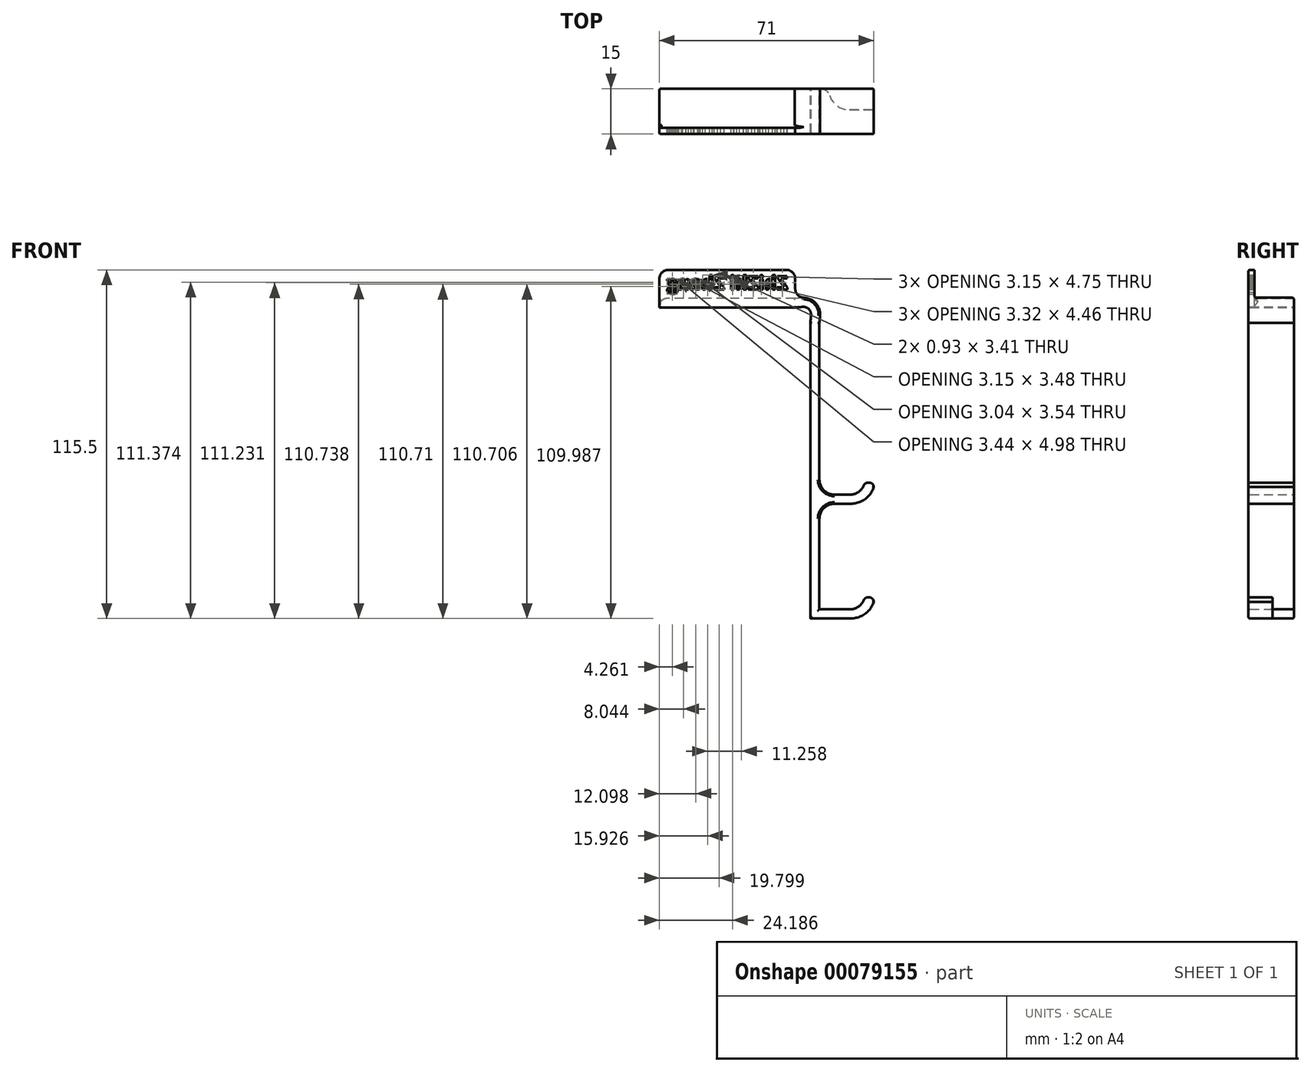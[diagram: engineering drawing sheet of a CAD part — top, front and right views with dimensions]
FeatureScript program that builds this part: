
annotation { "Feature Type Name" : "Feature", "Feature Type Description" : "" }
export const myFeature = defineFeature(function(context is Context, id is Id, definition is map)
    precondition{}
    {
        {
            var Q0;
            Q0=qCreatedBy(makeId("Front.planeOp"),FACE);
            var sketch = newSketch(context, id + "F0", { "sketchPlane" : qUnion([Q0])});
            skLineSegment(sketch, "E0.top", {"start": v(3, 3) * mm, "end": v(18, 3) * mm});
            skLineSegment(sketch, "E1.top", {"start": v(21, 7) * mm, "end": v(18, 7) * mm});
            skLineSegment(sketch, "E1.right", {"start": v(18, 3) * mm, "end": v(18, 7) * mm});
            skLineSegment(sketch, "E2", {"start": v(21, 7) * mm, "end": v(21, 0) * mm});
            skLineSegment(sketch, "E3", {"start": v(21, 0) * mm, "end": v(3, 0) * mm});
            skLineSegment(sketch, "E4.top", {"start": v(-5, 65) * mm, "end": v(-50, 65) * mm});
            skLineSegment(sketch, "E4.right", {"start": v(-50, 68) * mm, "end": v(-50, 65) * mm});
            skLineSegment(sketch, "E5", {"start": v(0, 65) * mm, "end": v(5.72, 70.72) * mm, "construction": true});
            skLineSegment(sketch, "E6", {"start": v(-5, 65) * mm, "end": v(0.5, 65.5) * mm});
            skLineSegment(sketch, "E7.MirrorCS", {"start": v(0, 60) * mm, "end": v(0.5, 65.5) * mm});
            skLineSegment(sketch, "E8", {"start": v(-5.14, 68) * mm, "end": v(3.81, 68.81) * mm});
            skLineSegment(sketch, "E9.MirrorCS", {"start": v(3, 59.86) * mm, "end": v(3.81, 68.81) * mm});
            skLineSegment(sketch, "E10", {"start": v(3, 3) * mm, "end": v(3, 59.86) * mm});
            skLineSegment(sketch, "E11.top", {"start": v(3, -35) * mm, "end": v(18, -35) * mm});
            skLineSegment(sketch, "E12.top", {"start": v(21, -31) * mm, "end": v(18, -31) * mm});
            skLineSegment(sketch, "E12.right", {"start": v(18, -35) * mm, "end": v(18, -31) * mm});
            skLineSegment(sketch, "E13", {"start": v(21, -31) * mm, "end": v(21, -38) * mm});
            skLineSegment(sketch, "E14", {"start": v(21, -38) * mm, "end": v(0, -38) * mm});
            skLineSegment(sketch, "E15", {"start": v(3, -35) * mm, "end": v(3, 0) * mm});
            skLineSegment(sketch, "E16", {"start": v(0, 60) * mm, "end": v(0, -38) * mm});
            skLineSegment(sketch, "E17", {"start": v(-5.14, 68) * mm, "end": v(-50, 68) * mm});
            skSolve(sketch);
        }
        {
            var Q0;
            Q0=qSketchRegion(id+"F0",true);
            extrude(context, id + "F1", {"entities" : qUnion([Q0]), "depth" : 15 * mm});
        }
        {
            var Q0;
            Q0=makeQuery(id+"F1.opExtrude","SWEPT_FACE",FACE,{"disambiguationData":[OSD([sQuery(id+"F0.wireOp",EDGE,"E11.top")])]});
            var sketch = newSketch(context, id + "F2", { "sketchPlane" : qUnion([Q0])});
            skLineSegment(sketch, "E18.0", {"start": v(21, -7) * mm, "end": v(21, 0) * mm});
            skLineSegment(sketch, "E19.bottom", {"start": v(6, 0) * mm, "end": v(21, 0) * mm});
            skLineSegment(sketch, "E19.top", {"start": v(6, -7) * mm, "end": v(21, -7) * mm});
            skLineSegment(sketch, "E19.left", {"start": v(6, 0) * mm, "end": v(6, -7) * mm});
            skLineSegment(sketch, "E19.right", {"start": v(21, 0) * mm, "end": v(21, -7) * mm});
            skPoint(sketch, "E20.orphan", {"position": v(21, -15) * mm});
            skSolve(sketch);
        }
        {
            var Q0;
            Q0 = qSketchRegion(id + "F2", true);
            extrude(context, id + "F3", {"entities" : qUnion([Q0]), "operationType" : NewBodyOperationType.REMOVE, "depth" : 25 * mm, "symmetric" : true});
        }
        {
            var Q0;
            Q0=makeQuery(id+"F1.opExtrude","SWEPT_EDGE",EDGE,{"disambiguationData":[OSD([sQuery(id+"F0.wireOp",EDGE,"VHxd6Wk6-jh9T-hKwV-plOy-LZrEurf6lyAQ.right"),sQuery(id+"F0.wireOp",EDGE,"E0.top")])]});
            var Q1;
            Q1=makeQuery(id+"F1.opExtrude","SWEPT_EDGE",EDGE,{"disambiguationData":[OSD([sQuery(id+"F0.wireOp",EDGE,"E0.top"),sQuery(id+"F0.wireOp",EDGE,"E1.right")])]});
            var Q2;
            Q2=makeQuery(id+"F1.opExtrude","SWEPT_EDGE",EDGE,{"disambiguationData":[OSD([sQuery(id+"F0.wireOp",EDGE,"E3"),sQuery(id+"F0.wireOp",EDGE,"E15")])]});
            var Q3;
            Q3=makeQuery(id+"F1.opExtrude","SWEPT_EDGE",EDGE,{"disambiguationData":[OSD([sQuery(id+"F0.wireOp",EDGE,"E11.top"),sQuery(id+"F0.wireOp",EDGE,"E12.right")])]});
            fillet(context, id + "F4", {"entities" : qUnion([Q0, Q1, Q2, Q3]), "radius" : 5 * mm, "tangentPropagation" : true, "allowEdgeOverflow" : false});
        }
        {
            var Q0;
            Q0=makeQuery(id+"F4.opFillet","BLEND_EDGE",EDGE,{"blendedFrom":[makeQuery(id+"F1.opExtrude","SWEPT_EDGE",EDGE,{"disambiguationData":[OSD([sQuery(id+"F0.wireOp",EDGE,"E0.top"),sQuery(id+"F0.wireOp",EDGE,"E1.right")])]}),makeQuery(id+"F1.opExtrude","SWEPT_FACE",FACE,{"disambiguationData":[OSD([sQuery(id+"F0.wireOp",EDGE,"E1.top")])]})],"blendedInto":[makeQuery(id+"F1.opExtrude","SWEPT_FACE",FACE,{"disambiguationData":[OSD([sQuery(id+"F0.wireOp",EDGE,"E1.top")])]})]});
            var Q1;
            Q1=makeQuery(id+"F1.opExtrude","SWEPT_EDGE",EDGE,{"disambiguationData":[OSD([sQuery(id+"F0.wireOp",EDGE,"E1.top"),sQuery(id+"F0.wireOp",EDGE,"E2")])]});
            var Q2;
            Q2=makeQuery(id+"F1.opExtrude","SWEPT_EDGE",EDGE,{"disambiguationData":[OSD([sQuery(id+"F0.wireOp",EDGE,"E12.top"),sQuery(id+"F0.wireOp",EDGE,"E13")])]});
            var Q3;
            Q3=makeQuery(id+"F4.opFillet","BLEND_EDGE",EDGE,{"blendedFrom":[makeQuery(id+"F1.opExtrude","SWEPT_EDGE",EDGE,{"disambiguationData":[OSD([sQuery(id+"F0.wireOp",EDGE,"E11.top"),sQuery(id+"F0.wireOp",EDGE,"E12.right")])]}),makeQuery(id+"F1.opExtrude","SWEPT_FACE",FACE,{"disambiguationData":[OSD([sQuery(id+"F0.wireOp",EDGE,"E12.top")])]})],"blendedInto":[makeQuery(id+"F1.opExtrude","SWEPT_FACE",FACE,{"disambiguationData":[OSD([sQuery(id+"F0.wireOp",EDGE,"E12.top")])]})]});
            fillet(context, id + "F5", {"entities" : qUnion([Q0, Q1, Q2, Q3]), "radius" : 1.5 * mm, "tangentPropagation" : true, "allowEdgeOverflow" : false});
        }
        {
            var Q0;
            Q0=makeQuery(id+"F1.opExtrude","SWEPT_EDGE",EDGE,{"disambiguationData":[OSD([sQuery(id+"F0.wireOp",EDGE,"E2"),sQuery(id+"F0.wireOp",EDGE,"E3")])]});
            var Q1;
            Q1=makeQuery(id+"F1.opExtrude","SWEPT_EDGE",EDGE,{"disambiguationData":[OSD([sQuery(id+"F0.wireOp",EDGE,"E13"),sQuery(id+"F0.wireOp",EDGE,"E14")])]});
            fillet(context, id + "F6", {"entities" : qUnion([Q0, Q1]), "radius" : 8 * mm, "tangentPropagation" : true, "allowEdgeOverflow" : false});
        }
        {
            var Q0;
            Q0=makeQuery(id+"F1.opExtrude","SWEPT_EDGE",EDGE,{"disambiguationData":[OSD([sQuery(id+"F0.wireOp",EDGE,"E6"),sQuery(id+"F0.wireOp",EDGE,"E7.MirrorCS")])]});
            fillet(context, id + "F7", {"entities" : qUnion([Q0]), "radius" : 2.5 * mm, "tangentPropagation" : true, "allowEdgeOverflow" : false});
        }
        {
            var Q0;
            Q0=makeQuery(id+"F1.opExtrude","SWEPT_EDGE",EDGE,{"disambiguationData":[OSD([sQuery(id+"F0.wireOp",EDGE,"E8"),sQuery(id+"F0.wireOp",EDGE,"E9.MirrorCS")])]});
            fillet(context, id + "F8", {"entities" : qUnion([Q0]), "radius" : 5.5 * mm, "tangentPropagation" : true, "allowEdgeOverflow" : false});
        }
        {
            var Q0;
            Q0=makeQuery(id+"F1.opExtrude","SWEPT_EDGE",EDGE,{"disambiguationData":[OSD([sQuery(id+"F0.wireOp",EDGE,"E4.right"),sQuery(id+"F0.wireOp",EDGE,"E17")])]});
            fillet(context, id + "F9", {"entities" : qUnion([Q0]), "radius" : 2.5 * mm, "tangentPropagation" : true, "allowEdgeOverflow" : false});
        }
        {
            var Q0;
            Q0=makeQuery(id+"FKw0b9sDwFtLhp3_1.boolean.opBoolean","COPY",EDGE,{"derivedFrom":makeQuery(id+"FKw0b9sDwFtLhp3_1.opExtrude","SWEPT_EDGE",EDGE,{"disambiguationData":[OSD([sQuery(id+"FaIadq1heUG16GC_1.wireOp",EDGE,"ajo2xejB-WB73-E7Yi-5oTq-upnxLA3L7wAk.top"),sQuery(id+"FaIadq1heUG16GC_1.wireOp",EDGE,"ajo2xejB-WB73-E7Yi-5oTq-upnxLA3L7wAk.left")])]})});
            var Q1;
            Q1=makeQuery(id+"F3.boolean.opBoolean","COPY",EDGE,{"derivedFrom":makeQuery(id+"F3.opExtrude","SWEPT_EDGE",EDGE,{"disambiguationData":[OSD([sQuery(id+"F2.wireOp",EDGE,"E19.top"),sQuery(id+"F2.wireOp",EDGE,"E19.left")])]})});
            fillet(context, id + "F10", {"entities" : qUnion([Q0, Q1]), "radius" : 7 * mm, "tangentPropagation" : true, "allowEdgeOverflow" : false});
        }
        {
            var Q0;
            Q0=makeQuery(id+"F1.opExtrude","CAP_FACE",FACE,{"disambiguationData":[OSD([sQuery(id+"F0.wireOp",EDGE,"E0.top"),sQuery(id+"F0.wireOp",EDGE,"E1.top"),sQuery(id+"F0.wireOp",EDGE,"E1.right"),sQuery(id+"F0.wireOp",EDGE,"E2"),sQuery(id+"F0.wireOp",EDGE,"E3"),sQuery(id+"F0.wireOp",EDGE,"E4.top"),sQuery(id+"F0.wireOp",EDGE,"E4.right"),sQuery(id+"F0.wireOp",EDGE,"E6"),sQuery(id+"F0.wireOp",EDGE,"E7.MirrorCS"),sQuery(id+"F0.wireOp",EDGE,"E8"),sQuery(id+"F0.wireOp",EDGE,"E9.MirrorCS"),sQuery(id+"F0.wireOp",EDGE,"E10"),sQuery(id+"F0.wireOp",EDGE,"E11.top"),sQuery(id+"F0.wireOp",EDGE,"E12.top"),sQuery(id+"F0.wireOp",EDGE,"E12.right"),sQuery(id+"F0.wireOp",EDGE,"E13"),sQuery(id+"F0.wireOp",EDGE,"E14"),sQuery(id+"F0.wireOp",EDGE,"E15"),sQuery(id+"F0.wireOp",EDGE,"E16"),sQuery(id+"F0.wireOp",EDGE,"E17")])],"isStart":false});
            var sketch = newSketch(context, id + "F11", { "sketchPlane" : qUnion([Q0])});
            skLineSegment(sketch, "E21.bottom", {"start": v(-5, 65.5) * mm, "end": v(-50, 65.5) * mm});
            skLineSegment(sketch, "E21.top", {"start": v(-5, 77.5) * mm, "end": v(-50, 77.5) * mm});
            skLineSegment(sketch, "E21.left", {"start": v(-50, 65.5) * mm, "end": v(-50, 77.5) * mm});
            skLineSegment(sketch, "E21.right", {"start": v(-5, 65.5) * mm, "end": v(-5, 77.5) * mm});
            skSolve(sketch);
        }
        {
            var Q0;
            Q0 = qSketchRegion(id + "F11", true);
            extrude(context, id + "F12", {"entities" : qUnion([Q0]), "operationType" : NewBodyOperationType.ADD, "oppositeDirection" : true, "depth" : 2 * mm});
        }
        {
            var Q0;
            Q0=makeQuery(id+"F12.opExtrude","SWEPT_EDGE",EDGE,{"disambiguationData":[OSD([sQuery(id+"F11.wireOp",EDGE,"E21.top"),sQuery(id+"F11.wireOp",EDGE,"E21.left")])]});
            var Q1;
            Q1=makeQuery(id+"F12.opExtrude","SWEPT_EDGE",EDGE,{"disambiguationData":[OSD([sQuery(id+"F11.wireOp",EDGE,"E21.top"),sQuery(id+"F11.wireOp",EDGE,"E21.right")])]});
            fillet(context, id + "F13", {"entities" : qUnion([Q0, Q1]), "radius" : 3 * mm, "tangentPropagation" : true, "allowEdgeOverflow" : false});
        }
        {
            var Q0;
            Q0=makeQuery(id+"F12.boolean.opBoolean","INTERSECT",EDGE,{"derivedFrom":[makeQuery(id+"F1.opExtrude","SWEPT_FACE",FACE,{"disambiguationData":[OSD([sQuery(id+"F0.wireOp",EDGE,"E17")])]}),makeQuery(id+"F12.opExtrude","CAP_FACE",FACE,{"disambiguationData":[OSD([sQuery(id+"F11.wireOp",EDGE,"E21.bottom"),sQuery(id+"F11.wireOp",EDGE,"E21.top"),sQuery(id+"F11.wireOp",EDGE,"E21.left"),sQuery(id+"F11.wireOp",EDGE,"E21.right")])],"isStart":false})]});
            var Q1;
            Q1=makeQuery(id+"F12.boolean.opBoolean","INTERSECT",EDGE,{"derivedFrom":[makeQuery(id+"F9.opFillet","BLEND_FACE",FACE,{"disambiguationData":[OSD([sQuery(id+"F0.wireOp",EDGE,"E4.right"),sQuery(id+"F0.wireOp",EDGE,"E17")])]}),makeQuery(id+"F12.opExtrude","CAP_FACE",FACE,{"disambiguationData":[OSD([sQuery(id+"F11.wireOp",EDGE,"E21.bottom"),sQuery(id+"F11.wireOp",EDGE,"E21.top"),sQuery(id+"F11.wireOp",EDGE,"E21.left"),sQuery(id+"F11.wireOp",EDGE,"E21.right")])],"isStart":false})]});
            fillet(context, id + "F14", {"entities" : qUnion([Q0, Q1]), "radius" : 1 * mm, "tangentPropagation" : true, "allowEdgeOverflow" : false});
        }
        {
            var Q0;
            Q0=makeQuery(id+"F12.boolean.opBoolean","INTERSECT",EDGE,{"derivedFrom":[makeQuery(id+"F1.opExtrude","SWEPT_FACE",FACE,{"disambiguationData":[OSD([sQuery(id+"F0.wireOp",EDGE,"E8")])]}),makeQuery(id+"F12.opExtrude","SWEPT_FACE",FACE,{"disambiguationData":[OSD([sQuery(id+"F11.wireOp",EDGE,"E21.right")])]})]});
            fillet(context, id + "F15", {"entities" : qUnion([Q0]), "radius" : 3 * mm, "tangentPropagation" : true, "allowEdgeOverflow" : false});
        }
        {
            var Q0;
            Q0=makeQuery(id+"F10.opFillet","BLEND_EDGE",EDGE,{"blendedFrom":[makeQuery(id+"FKw0b9sDwFtLhp3_1.boolean.opBoolean","COPY",EDGE,{"derivedFrom":makeQuery(id+"FKw0b9sDwFtLhp3_1.opExtrude","SWEPT_EDGE",EDGE,{"disambiguationData":[OSD([sQuery(id+"FaIadq1heUG16GC_1.wireOp",EDGE,"ajo2xejB-WB73-E7Yi-5oTq-upnxLA3L7wAk.top"),sQuery(id+"FaIadq1heUG16GC_1.wireOp",EDGE,"ajo2xejB-WB73-E7Yi-5oTq-upnxLA3L7wAk.left")])]})}),makeQuery(id+"F1.opExtrude","CAP_FACE",FACE,{"disambiguationData":[OSD([sQuery(id+"F0.wireOp",EDGE,"E0.top"),sQuery(id+"F0.wireOp",EDGE,"E1.top"),sQuery(id+"F0.wireOp",EDGE,"E1.right"),sQuery(id+"F0.wireOp",EDGE,"E2"),sQuery(id+"F0.wireOp",EDGE,"E3"),sQuery(id+"F0.wireOp",EDGE,"E4.top"),sQuery(id+"F0.wireOp",EDGE,"E4.right"),sQuery(id+"F0.wireOp",EDGE,"E6"),sQuery(id+"F0.wireOp",EDGE,"E7.MirrorCS"),sQuery(id+"F0.wireOp",EDGE,"E8"),sQuery(id+"F0.wireOp",EDGE,"E9.MirrorCS"),sQuery(id+"F0.wireOp",EDGE,"E10"),sQuery(id+"F0.wireOp",EDGE,"E11.top"),sQuery(id+"F0.wireOp",EDGE,"E12.top"),sQuery(id+"F0.wireOp",EDGE,"E12.right"),sQuery(id+"F0.wireOp",EDGE,"E13"),sQuery(id+"F0.wireOp",EDGE,"E14"),sQuery(id+"F0.wireOp",EDGE,"E15"),sQuery(id+"F0.wireOp",EDGE,"E16"),sQuery(id+"F0.wireOp",EDGE,"E17")])],"isStart":false})],"blendedInto":[makeQuery(id+"F1.opExtrude","CAP_FACE",FACE,{"disambiguationData":[OSD([sQuery(id+"F0.wireOp",EDGE,"E0.top"),sQuery(id+"F0.wireOp",EDGE,"E1.top"),sQuery(id+"F0.wireOp",EDGE,"E1.right"),sQuery(id+"F0.wireOp",EDGE,"E2"),sQuery(id+"F0.wireOp",EDGE,"E3"),sQuery(id+"F0.wireOp",EDGE,"E4.top"),sQuery(id+"F0.wireOp",EDGE,"E4.right"),sQuery(id+"F0.wireOp",EDGE,"E6"),sQuery(id+"F0.wireOp",EDGE,"E7.MirrorCS"),sQuery(id+"F0.wireOp",EDGE,"E8"),sQuery(id+"F0.wireOp",EDGE,"E9.MirrorCS"),sQuery(id+"F0.wireOp",EDGE,"E10"),sQuery(id+"F0.wireOp",EDGE,"E11.top"),sQuery(id+"F0.wireOp",EDGE,"E12.top"),sQuery(id+"F0.wireOp",EDGE,"E12.right"),sQuery(id+"F0.wireOp",EDGE,"E13"),sQuery(id+"F0.wireOp",EDGE,"E14"),sQuery(id+"F0.wireOp",EDGE,"E15"),sQuery(id+"F0.wireOp",EDGE,"E16"),sQuery(id+"F0.wireOp",EDGE,"E17")])],"isStart":false})]});
            var Q1;
            Q1=makeQuery(id+"F10.opFillet","BLEND_EDGE",EDGE,{"blendedFrom":[makeQuery(id+"F3.boolean.opBoolean","COPY",EDGE,{"derivedFrom":makeQuery(id+"F3.opExtrude","SWEPT_EDGE",EDGE,{"disambiguationData":[OSD([sQuery(id+"F2.wireOp",EDGE,"E19.top"),sQuery(id+"F2.wireOp",EDGE,"E19.left")])]})}),makeQuery(id+"F1.opExtrude","CAP_FACE",FACE,{"disambiguationData":[OSD([sQuery(id+"F0.wireOp",EDGE,"E0.top"),sQuery(id+"F0.wireOp",EDGE,"E1.top"),sQuery(id+"F0.wireOp",EDGE,"E1.right"),sQuery(id+"F0.wireOp",EDGE,"E2"),sQuery(id+"F0.wireOp",EDGE,"E3"),sQuery(id+"F0.wireOp",EDGE,"E4.top"),sQuery(id+"F0.wireOp",EDGE,"E4.right"),sQuery(id+"F0.wireOp",EDGE,"E6"),sQuery(id+"F0.wireOp",EDGE,"E7.MirrorCS"),sQuery(id+"F0.wireOp",EDGE,"E8"),sQuery(id+"F0.wireOp",EDGE,"E9.MirrorCS"),sQuery(id+"F0.wireOp",EDGE,"E10"),sQuery(id+"F0.wireOp",EDGE,"E11.top"),sQuery(id+"F0.wireOp",EDGE,"E12.top"),sQuery(id+"F0.wireOp",EDGE,"E12.right"),sQuery(id+"F0.wireOp",EDGE,"E13"),sQuery(id+"F0.wireOp",EDGE,"E14"),sQuery(id+"F0.wireOp",EDGE,"E15"),sQuery(id+"F0.wireOp",EDGE,"E16"),sQuery(id+"F0.wireOp",EDGE,"E17")])],"isStart":true})],"blendedInto":[makeQuery(id+"F1.opExtrude","CAP_FACE",FACE,{"disambiguationData":[OSD([sQuery(id+"F0.wireOp",EDGE,"E0.top"),sQuery(id+"F0.wireOp",EDGE,"E1.top"),sQuery(id+"F0.wireOp",EDGE,"E1.right"),sQuery(id+"F0.wireOp",EDGE,"E2"),sQuery(id+"F0.wireOp",EDGE,"E3"),sQuery(id+"F0.wireOp",EDGE,"E4.top"),sQuery(id+"F0.wireOp",EDGE,"E4.right"),sQuery(id+"F0.wireOp",EDGE,"E6"),sQuery(id+"F0.wireOp",EDGE,"E7.MirrorCS"),sQuery(id+"F0.wireOp",EDGE,"E8"),sQuery(id+"F0.wireOp",EDGE,"E9.MirrorCS"),sQuery(id+"F0.wireOp",EDGE,"E10"),sQuery(id+"F0.wireOp",EDGE,"E11.top"),sQuery(id+"F0.wireOp",EDGE,"E12.top"),sQuery(id+"F0.wireOp",EDGE,"E12.right"),sQuery(id+"F0.wireOp",EDGE,"E13"),sQuery(id+"F0.wireOp",EDGE,"E14"),sQuery(id+"F0.wireOp",EDGE,"E15"),sQuery(id+"F0.wireOp",EDGE,"E16"),sQuery(id+"F0.wireOp",EDGE,"E17")])],"isStart":true})]});
            fillet(context, id + "F16", {"entities" : qUnion([Q0, Q1]), "radius" : 3 * mm, "tangentPropagation" : true, "allowEdgeOverflow" : false});
        }
        {
            var Q0;
            Q0=makeQuery(id+"F12.opExtrude","CAP_FACE",FACE,{"disambiguationData":[OSD([sQuery(id+"F11.wireOp",EDGE,"E21.bottom"),sQuery(id+"F11.wireOp",EDGE,"E21.top"),sQuery(id+"F11.wireOp",EDGE,"E21.left"),sQuery(id+"F11.wireOp",EDGE,"E21.right")])],"isStart":false});
            var sketch = newSketch(context, id + "F17", { "sketchPlane" : qUnion([Q0])});
            skText(sketch, "E22", { "text": "ZhiZhi Zhang", "fontName": "OpenSans-Bold.ttf"});
            const initialGuessF17  = {"E22": [0.0075, 0.071, 1, 0, 0.0045]};
            skSetInitialGuess(sketch, initialGuessF17);
            skSolve(sketch);
        }
        {
            var Q0;
            Q0 = qSketchRegion(id + "F17", true);
            extrude(context, id + "F18", {"entities" : qUnion([Q0]), "operationType" : NewBodyOperationType.REMOVE, "endBound" : BoundingType.UP_TO_NEXT, "oppositeDirection" : true, "depth" : 25 * mm});
        }
        {
            var Q0;
            Q0=makeQuery(id+"F1.opExtrude","CAP_EDGE",EDGE,{"disambiguationData":[OSD([sQuery(id+"F0.wireOp",EDGE,"E10")])],"isStart":true});
            var Q1;
            {var subQ0=sQuery(id+"F0.wireOp",EDGE,"E10");var subQ1=sQuery(id+"F0.wireOp",EDGE,"E0.top");Q1=makeQuery(id+"F4.opFillet","BLEND_EDGE",EDGE,{"blendedFrom":[makeQuery(id+"F1.opExtrude","SWEPT_EDGE",EDGE,{"disambiguationData":[OSD([subQ1,subQ0])]}),makeQuery(id+"F1.opExtrude","CAP_FACE",FACE,{"disambiguationData":[OSD([subQ1,sQuery(id+"F0.wireOp",EDGE,"E1.top"),sQuery(id+"F0.wireOp",EDGE,"E1.right"),sQuery(id+"F0.wireOp",EDGE,"E2"),sQuery(id+"F0.wireOp",EDGE,"E3"),sQuery(id+"F0.wireOp",EDGE,"E4.top"),sQuery(id+"F0.wireOp",EDGE,"E4.right"),sQuery(id+"F0.wireOp",EDGE,"E6"),sQuery(id+"F0.wireOp",EDGE,"E7.MirrorCS"),sQuery(id+"F0.wireOp",EDGE,"E8"),sQuery(id+"F0.wireOp",EDGE,"E9.MirrorCS"),subQ0,sQuery(id+"F0.wireOp",EDGE,"E11.top"),sQuery(id+"F0.wireOp",EDGE,"E12.top"),sQuery(id+"F0.wireOp",EDGE,"E12.right"),sQuery(id+"F0.wireOp",EDGE,"E13"),sQuery(id+"F0.wireOp",EDGE,"E14"),sQuery(id+"F0.wireOp",EDGE,"E15"),sQuery(id+"F0.wireOp",EDGE,"E16"),sQuery(id+"F0.wireOp",EDGE,"E17")])],"isStart":true})],"blendedInto":[makeQuery(id+"F1.opExtrude","CAP_FACE",FACE,{"disambiguationData":[OSD([subQ1,sQuery(id+"F0.wireOp",EDGE,"E1.top"),sQuery(id+"F0.wireOp",EDGE,"E1.right"),sQuery(id+"F0.wireOp",EDGE,"E2"),sQuery(id+"F0.wireOp",EDGE,"E3"),sQuery(id+"F0.wireOp",EDGE,"E4.top"),sQuery(id+"F0.wireOp",EDGE,"E4.right"),sQuery(id+"F0.wireOp",EDGE,"E6"),sQuery(id+"F0.wireOp",EDGE,"E7.MirrorCS"),sQuery(id+"F0.wireOp",EDGE,"E8"),sQuery(id+"F0.wireOp",EDGE,"E9.MirrorCS"),subQ0,sQuery(id+"F0.wireOp",EDGE,"E11.top"),sQuery(id+"F0.wireOp",EDGE,"E12.top"),sQuery(id+"F0.wireOp",EDGE,"E12.right"),sQuery(id+"F0.wireOp",EDGE,"E13"),sQuery(id+"F0.wireOp",EDGE,"E14"),sQuery(id+"F0.wireOp",EDGE,"E15"),sQuery(id+"F0.wireOp",EDGE,"E16"),sQuery(id+"F0.wireOp",EDGE,"E17")])],"isStart":true})]});}
            var Q2;
            Q2=makeQuery(id+"F1.opExtrude","CAP_EDGE",EDGE,{"disambiguationData":[OSD([sQuery(id+"F0.wireOp",EDGE,"E9.MirrorCS")])],"isStart":true});
            var Q3;
            {var subQ0=sQuery(id+"F0.wireOp",EDGE,"E9.MirrorCS");var subQ1=sQuery(id+"F0.wireOp",EDGE,"E8");Q3=makeQuery(id+"F8.opFillet","BLEND_EDGE",EDGE,{"blendedFrom":[makeQuery(id+"F1.opExtrude","SWEPT_EDGE",EDGE,{"disambiguationData":[OSD([subQ1,subQ0])]}),makeQuery(id+"F1.opExtrude","CAP_FACE",FACE,{"disambiguationData":[OSD([sQuery(id+"F0.wireOp",EDGE,"E0.top"),sQuery(id+"F0.wireOp",EDGE,"E1.top"),sQuery(id+"F0.wireOp",EDGE,"E1.right"),sQuery(id+"F0.wireOp",EDGE,"E2"),sQuery(id+"F0.wireOp",EDGE,"E3"),sQuery(id+"F0.wireOp",EDGE,"E4.top"),sQuery(id+"F0.wireOp",EDGE,"E4.right"),sQuery(id+"F0.wireOp",EDGE,"E6"),sQuery(id+"F0.wireOp",EDGE,"E7.MirrorCS"),subQ1,subQ0,sQuery(id+"F0.wireOp",EDGE,"E10"),sQuery(id+"F0.wireOp",EDGE,"E11.top"),sQuery(id+"F0.wireOp",EDGE,"E12.top"),sQuery(id+"F0.wireOp",EDGE,"E12.right"),sQuery(id+"F0.wireOp",EDGE,"E13"),sQuery(id+"F0.wireOp",EDGE,"E14"),sQuery(id+"F0.wireOp",EDGE,"E15"),sQuery(id+"F0.wireOp",EDGE,"E16"),sQuery(id+"F0.wireOp",EDGE,"E17")])],"isStart":true})],"blendedInto":[makeQuery(id+"F1.opExtrude","CAP_FACE",FACE,{"disambiguationData":[OSD([sQuery(id+"F0.wireOp",EDGE,"E0.top"),sQuery(id+"F0.wireOp",EDGE,"E1.top"),sQuery(id+"F0.wireOp",EDGE,"E1.right"),sQuery(id+"F0.wireOp",EDGE,"E2"),sQuery(id+"F0.wireOp",EDGE,"E3"),sQuery(id+"F0.wireOp",EDGE,"E4.top"),sQuery(id+"F0.wireOp",EDGE,"E4.right"),sQuery(id+"F0.wireOp",EDGE,"E6"),sQuery(id+"F0.wireOp",EDGE,"E7.MirrorCS"),subQ1,subQ0,sQuery(id+"F0.wireOp",EDGE,"E10"),sQuery(id+"F0.wireOp",EDGE,"E11.top"),sQuery(id+"F0.wireOp",EDGE,"E12.top"),sQuery(id+"F0.wireOp",EDGE,"E12.right"),sQuery(id+"F0.wireOp",EDGE,"E13"),sQuery(id+"F0.wireOp",EDGE,"E14"),sQuery(id+"F0.wireOp",EDGE,"E15"),sQuery(id+"F0.wireOp",EDGE,"E16"),sQuery(id+"F0.wireOp",EDGE,"E17")])],"isStart":true})]});}
            var Q4;
            Q4=makeQuery(id+"F1.opExtrude","CAP_EDGE",EDGE,{"disambiguationData":[OSD([sQuery(id+"F0.wireOp",EDGE,"E8")])],"isStart":true});
            var Q5;
            Q5=makeQuery(id+"F1.opExtrude","CAP_EDGE",EDGE,{"disambiguationData":[OSD([sQuery(id+"F0.wireOp",EDGE,"E17")])],"isStart":true});
            var Q6;
            {var subQ0=sQuery(id+"F0.wireOp",EDGE,"E17");var subQ1=sQuery(id+"F0.wireOp",EDGE,"E4.right");Q6=makeQuery(id+"F9.opFillet","BLEND_EDGE",EDGE,{"blendedFrom":[makeQuery(id+"F1.opExtrude","SWEPT_EDGE",EDGE,{"disambiguationData":[OSD([subQ1,subQ0])]}),makeQuery(id+"F1.opExtrude","CAP_FACE",FACE,{"disambiguationData":[OSD([sQuery(id+"F0.wireOp",EDGE,"E0.top"),sQuery(id+"F0.wireOp",EDGE,"E1.top"),sQuery(id+"F0.wireOp",EDGE,"E1.right"),sQuery(id+"F0.wireOp",EDGE,"E2"),sQuery(id+"F0.wireOp",EDGE,"E3"),sQuery(id+"F0.wireOp",EDGE,"E4.top"),subQ1,sQuery(id+"F0.wireOp",EDGE,"E6"),sQuery(id+"F0.wireOp",EDGE,"E7.MirrorCS"),sQuery(id+"F0.wireOp",EDGE,"E8"),sQuery(id+"F0.wireOp",EDGE,"E9.MirrorCS"),sQuery(id+"F0.wireOp",EDGE,"E10"),sQuery(id+"F0.wireOp",EDGE,"E11.top"),sQuery(id+"F0.wireOp",EDGE,"E12.top"),sQuery(id+"F0.wireOp",EDGE,"E12.right"),sQuery(id+"F0.wireOp",EDGE,"E13"),sQuery(id+"F0.wireOp",EDGE,"E14"),sQuery(id+"F0.wireOp",EDGE,"E15"),sQuery(id+"F0.wireOp",EDGE,"E16"),subQ0])],"isStart":true})],"blendedInto":[makeQuery(id+"F1.opExtrude","CAP_FACE",FACE,{"disambiguationData":[OSD([sQuery(id+"F0.wireOp",EDGE,"E0.top"),sQuery(id+"F0.wireOp",EDGE,"E1.top"),sQuery(id+"F0.wireOp",EDGE,"E1.right"),sQuery(id+"F0.wireOp",EDGE,"E2"),sQuery(id+"F0.wireOp",EDGE,"E3"),sQuery(id+"F0.wireOp",EDGE,"E4.top"),subQ1,sQuery(id+"F0.wireOp",EDGE,"E6"),sQuery(id+"F0.wireOp",EDGE,"E7.MirrorCS"),sQuery(id+"F0.wireOp",EDGE,"E8"),sQuery(id+"F0.wireOp",EDGE,"E9.MirrorCS"),sQuery(id+"F0.wireOp",EDGE,"E10"),sQuery(id+"F0.wireOp",EDGE,"E11.top"),sQuery(id+"F0.wireOp",EDGE,"E12.top"),sQuery(id+"F0.wireOp",EDGE,"E12.right"),sQuery(id+"F0.wireOp",EDGE,"E13"),sQuery(id+"F0.wireOp",EDGE,"E14"),sQuery(id+"F0.wireOp",EDGE,"E15"),sQuery(id+"F0.wireOp",EDGE,"E16"),subQ0])],"isStart":true})]});}
            var Q7;
            Q7=makeQuery(id+"F1.opExtrude","CAP_EDGE",EDGE,{"disambiguationData":[OSD([sQuery(id+"F0.wireOp",EDGE,"E4.top")])],"isStart":true});
            var Q8;
            Q8=makeQuery(id+"F1.opExtrude","CAP_EDGE",EDGE,{"disambiguationData":[OSD([sQuery(id+"F0.wireOp",EDGE,"E4.right")])],"isStart":true});
            var Q9;
            Q9=makeQuery(id+"F1.opExtrude","CAP_EDGE",EDGE,{"disambiguationData":[OSD([sQuery(id+"F0.wireOp",EDGE,"E6")])],"isStart":true});
            var Q10;
            {var subQ0=sQuery(id+"F0.wireOp",EDGE,"E7.MirrorCS");var subQ1=sQuery(id+"F0.wireOp",EDGE,"E6");Q10=makeQuery(id+"F7.opFillet","BLEND_EDGE",EDGE,{"blendedFrom":[makeQuery(id+"F1.opExtrude","SWEPT_EDGE",EDGE,{"disambiguationData":[OSD([subQ1,subQ0])]}),makeQuery(id+"F1.opExtrude","CAP_FACE",FACE,{"disambiguationData":[OSD([sQuery(id+"F0.wireOp",EDGE,"E0.top"),sQuery(id+"F0.wireOp",EDGE,"E1.top"),sQuery(id+"F0.wireOp",EDGE,"E1.right"),sQuery(id+"F0.wireOp",EDGE,"E2"),sQuery(id+"F0.wireOp",EDGE,"E3"),sQuery(id+"F0.wireOp",EDGE,"E4.top"),sQuery(id+"F0.wireOp",EDGE,"E4.right"),subQ1,subQ0,sQuery(id+"F0.wireOp",EDGE,"E8"),sQuery(id+"F0.wireOp",EDGE,"E9.MirrorCS"),sQuery(id+"F0.wireOp",EDGE,"E10"),sQuery(id+"F0.wireOp",EDGE,"E11.top"),sQuery(id+"F0.wireOp",EDGE,"E12.top"),sQuery(id+"F0.wireOp",EDGE,"E12.right"),sQuery(id+"F0.wireOp",EDGE,"E13"),sQuery(id+"F0.wireOp",EDGE,"E14"),sQuery(id+"F0.wireOp",EDGE,"E15"),sQuery(id+"F0.wireOp",EDGE,"E16"),sQuery(id+"F0.wireOp",EDGE,"E17")])],"isStart":true})],"blendedInto":[makeQuery(id+"F1.opExtrude","CAP_FACE",FACE,{"disambiguationData":[OSD([sQuery(id+"F0.wireOp",EDGE,"E0.top"),sQuery(id+"F0.wireOp",EDGE,"E1.top"),sQuery(id+"F0.wireOp",EDGE,"E1.right"),sQuery(id+"F0.wireOp",EDGE,"E2"),sQuery(id+"F0.wireOp",EDGE,"E3"),sQuery(id+"F0.wireOp",EDGE,"E4.top"),sQuery(id+"F0.wireOp",EDGE,"E4.right"),subQ1,subQ0,sQuery(id+"F0.wireOp",EDGE,"E8"),sQuery(id+"F0.wireOp",EDGE,"E9.MirrorCS"),sQuery(id+"F0.wireOp",EDGE,"E10"),sQuery(id+"F0.wireOp",EDGE,"E11.top"),sQuery(id+"F0.wireOp",EDGE,"E12.top"),sQuery(id+"F0.wireOp",EDGE,"E12.right"),sQuery(id+"F0.wireOp",EDGE,"E13"),sQuery(id+"F0.wireOp",EDGE,"E14"),sQuery(id+"F0.wireOp",EDGE,"E15"),sQuery(id+"F0.wireOp",EDGE,"E16"),sQuery(id+"F0.wireOp",EDGE,"E17")])],"isStart":true})]});}
            var Q11;
            Q11=makeQuery(id+"F1.opExtrude","CAP_EDGE",EDGE,{"disambiguationData":[OSD([sQuery(id+"F0.wireOp",EDGE,"E7.MirrorCS")])],"isStart":true});
            var Q12;
            Q12=makeQuery(id+"F1.opExtrude","CAP_EDGE",EDGE,{"disambiguationData":[OSD([sQuery(id+"F0.wireOp",EDGE,"E16")])],"isStart":true});
            var Q13;
            Q13=makeQuery(id+"F1.opExtrude","CAP_EDGE",EDGE,{"disambiguationData":[OSD([sQuery(id+"F0.wireOp",EDGE,"E14")])],"isStart":true});
            var Q14;
            {var subQ0=sQuery(id+"F0.wireOp",EDGE,"E14");Q14=makeQuery(id+"F16.opFillet","BLEND_EDGE",EDGE,{"blendedFrom":[makeQuery(id+"F10.opFillet","BLEND_EDGE",EDGE,{"blendedFrom":[makeQuery(id+"F3.boolean.opBoolean","COPY",EDGE,{"derivedFrom":makeQuery(id+"F3.opExtrude","SWEPT_EDGE",EDGE,{"disambiguationData":[OSD([sQuery(id+"F2.wireOp",EDGE,"E19.top"),sQuery(id+"F2.wireOp",EDGE,"E19.left")])]})}),makeQuery(id+"F1.opExtrude","CAP_FACE",FACE,{"disambiguationData":[OSD([sQuery(id+"F0.wireOp",EDGE,"E0.top"),sQuery(id+"F0.wireOp",EDGE,"E1.top"),sQuery(id+"F0.wireOp",EDGE,"E1.right"),sQuery(id+"F0.wireOp",EDGE,"E2"),sQuery(id+"F0.wireOp",EDGE,"E3"),sQuery(id+"F0.wireOp",EDGE,"E4.top"),sQuery(id+"F0.wireOp",EDGE,"E4.right"),sQuery(id+"F0.wireOp",EDGE,"E6"),sQuery(id+"F0.wireOp",EDGE,"E7.MirrorCS"),sQuery(id+"F0.wireOp",EDGE,"E8"),sQuery(id+"F0.wireOp",EDGE,"E9.MirrorCS"),sQuery(id+"F0.wireOp",EDGE,"E10"),sQuery(id+"F0.wireOp",EDGE,"E11.top"),sQuery(id+"F0.wireOp",EDGE,"E12.top"),sQuery(id+"F0.wireOp",EDGE,"E12.right"),sQuery(id+"F0.wireOp",EDGE,"E13"),subQ0,sQuery(id+"F0.wireOp",EDGE,"E15"),sQuery(id+"F0.wireOp",EDGE,"E16"),sQuery(id+"F0.wireOp",EDGE,"E17")])],"isStart":true})],"blendedInto":[makeQuery(id+"F1.opExtrude","CAP_FACE",FACE,{"disambiguationData":[OSD([sQuery(id+"F0.wireOp",EDGE,"E0.top"),sQuery(id+"F0.wireOp",EDGE,"E1.top"),sQuery(id+"F0.wireOp",EDGE,"E1.right"),sQuery(id+"F0.wireOp",EDGE,"E2"),sQuery(id+"F0.wireOp",EDGE,"E3"),sQuery(id+"F0.wireOp",EDGE,"E4.top"),sQuery(id+"F0.wireOp",EDGE,"E4.right"),sQuery(id+"F0.wireOp",EDGE,"E6"),sQuery(id+"F0.wireOp",EDGE,"E7.MirrorCS"),sQuery(id+"F0.wireOp",EDGE,"E8"),sQuery(id+"F0.wireOp",EDGE,"E9.MirrorCS"),sQuery(id+"F0.wireOp",EDGE,"E10"),sQuery(id+"F0.wireOp",EDGE,"E11.top"),sQuery(id+"F0.wireOp",EDGE,"E12.top"),sQuery(id+"F0.wireOp",EDGE,"E12.right"),sQuery(id+"F0.wireOp",EDGE,"E13"),subQ0,sQuery(id+"F0.wireOp",EDGE,"E15"),sQuery(id+"F0.wireOp",EDGE,"E16"),sQuery(id+"F0.wireOp",EDGE,"E17")])],"isStart":true})]}),makeQuery(id+"F1.opExtrude","SWEPT_FACE",FACE,{"disambiguationData":[OSD([subQ0])]})],"blendedInto":[makeQuery(id+"F1.opExtrude","SWEPT_FACE",FACE,{"disambiguationData":[OSD([subQ0])]})]});}
            var Q15;
            Q15=makeQuery(id+"F10.opFillet","BLEND_EDGE",EDGE,{"blendedFrom":[makeQuery(id+"F3.boolean.opBoolean","COPY",EDGE,{"derivedFrom":makeQuery(id+"F3.opExtrude","SWEPT_EDGE",EDGE,{"disambiguationData":[OSD([sQuery(id+"F2.wireOp",EDGE,"E19.top"),sQuery(id+"F2.wireOp",EDGE,"E19.left")])]})}),makeQuery(id+"F1.opExtrude","SWEPT_FACE",FACE,{"disambiguationData":[OSD([sQuery(id+"F0.wireOp",EDGE,"E14")])]})],"blendedInto":[makeQuery(id+"F1.opExtrude","SWEPT_FACE",FACE,{"disambiguationData":[OSD([sQuery(id+"F0.wireOp",EDGE,"E14")])]})]});
            var Q16;
            Q16=makeQuery(id+"F6.opFillet","BLEND_EDGE",EDGE,{"blendedFrom":[makeQuery(id+"F1.opExtrude","SWEPT_EDGE",EDGE,{"disambiguationData":[OSD([sQuery(id+"F0.wireOp",EDGE,"E13"),sQuery(id+"F0.wireOp",EDGE,"E14")])]}),makeQuery(id+"F3.boolean.opBoolean","COPY",FACE,{"derivedFrom":makeQuery(id+"F3.opExtrude","SWEPT_FACE",FACE,{"disambiguationData":[OSD([sQuery(id+"F2.wireOp",EDGE,"E19.top")])]})})],"blendedInto":[makeQuery(id+"F3.boolean.opBoolean","COPY",FACE,{"derivedFrom":makeQuery(id+"F3.opExtrude","SWEPT_FACE",FACE,{"disambiguationData":[OSD([sQuery(id+"F2.wireOp",EDGE,"E19.top")])]})})]});
            var Q17;
            Q17=makeQuery(id+"F3.boolean.opBoolean","INTERSECT",EDGE,{"derivedFrom":[makeQuery(id+"F1.opExtrude","SWEPT_FACE",FACE,{"disambiguationData":[OSD([sQuery(id+"F0.wireOp",EDGE,"E14")])]}),makeQuery(id+"F3.opExtrude","SWEPT_FACE",FACE,{"disambiguationData":[OSD([sQuery(id+"F2.wireOp",EDGE,"E19.top")])]})]});
            var Q18;
            Q18=makeQuery(id+"F5.opFillet","BLEND_EDGE",EDGE,{"blendedFrom":[makeQuery(id+"F1.opExtrude","SWEPT_EDGE",EDGE,{"disambiguationData":[OSD([sQuery(id+"F0.wireOp",EDGE,"E12.top"),sQuery(id+"F0.wireOp",EDGE,"E13")])]}),makeQuery(id+"F3.boolean.opBoolean","COPY",FACE,{"derivedFrom":makeQuery(id+"F3.opExtrude","SWEPT_FACE",FACE,{"disambiguationData":[OSD([sQuery(id+"F2.wireOp",EDGE,"E19.top")])]})})],"blendedInto":[makeQuery(id+"F3.boolean.opBoolean","COPY",FACE,{"derivedFrom":makeQuery(id+"F3.opExtrude","SWEPT_FACE",FACE,{"disambiguationData":[OSD([sQuery(id+"F2.wireOp",EDGE,"E19.top")])]})})]});
            var Q19;
            Q19=makeQuery(id+"F3.boolean.opBoolean","INTERSECT",EDGE,{"derivedFrom":[makeQuery(id+"F1.opExtrude","SWEPT_FACE",FACE,{"disambiguationData":[OSD([sQuery(id+"F0.wireOp",EDGE,"E12.top")])]}),makeQuery(id+"F3.opExtrude","SWEPT_FACE",FACE,{"disambiguationData":[OSD([sQuery(id+"F2.wireOp",EDGE,"E19.top")])]})]});
            var Q20;
            Q20=makeQuery(id+"F5.opFillet","BLEND_EDGE",EDGE,{"blendedFrom":[makeQuery(id+"F4.opFillet","BLEND_EDGE",EDGE,{"blendedFrom":[makeQuery(id+"F1.opExtrude","SWEPT_EDGE",EDGE,{"disambiguationData":[OSD([sQuery(id+"F0.wireOp",EDGE,"E11.top"),sQuery(id+"F0.wireOp",EDGE,"E12.right")])]}),makeQuery(id+"F1.opExtrude","SWEPT_FACE",FACE,{"disambiguationData":[OSD([sQuery(id+"F0.wireOp",EDGE,"E12.top")])]})],"blendedInto":[makeQuery(id+"F1.opExtrude","SWEPT_FACE",FACE,{"disambiguationData":[OSD([sQuery(id+"F0.wireOp",EDGE,"E12.top")])]})]}),makeQuery(id+"F3.boolean.opBoolean","COPY",FACE,{"derivedFrom":makeQuery(id+"F3.opExtrude","SWEPT_FACE",FACE,{"disambiguationData":[OSD([sQuery(id+"F2.wireOp",EDGE,"E19.top")])]})})],"blendedInto":[makeQuery(id+"F3.boolean.opBoolean","COPY",FACE,{"derivedFrom":makeQuery(id+"F3.opExtrude","SWEPT_FACE",FACE,{"disambiguationData":[OSD([sQuery(id+"F2.wireOp",EDGE,"E19.top")])]})})]});
            var Q21;
            Q21=makeQuery(id+"F4.opFillet","BLEND_EDGE",EDGE,{"blendedFrom":[makeQuery(id+"F1.opExtrude","SWEPT_EDGE",EDGE,{"disambiguationData":[OSD([sQuery(id+"F0.wireOp",EDGE,"E11.top"),sQuery(id+"F0.wireOp",EDGE,"E12.right")])]}),makeQuery(id+"F3.boolean.opBoolean","COPY",FACE,{"derivedFrom":makeQuery(id+"F3.opExtrude","SWEPT_FACE",FACE,{"disambiguationData":[OSD([sQuery(id+"F2.wireOp",EDGE,"E19.top")])]})})],"blendedInto":[makeQuery(id+"F3.boolean.opBoolean","COPY",FACE,{"derivedFrom":makeQuery(id+"F3.opExtrude","SWEPT_FACE",FACE,{"disambiguationData":[OSD([sQuery(id+"F2.wireOp",EDGE,"E19.top")])]})})]});
            var Q22;
            Q22=makeQuery(id+"F10.opFillet","BLEND_EDGE",EDGE,{"blendedFrom":[makeQuery(id+"F3.boolean.opBoolean","COPY",EDGE,{"derivedFrom":makeQuery(id+"F3.opExtrude","SWEPT_EDGE",EDGE,{"disambiguationData":[OSD([sQuery(id+"F2.wireOp",EDGE,"E19.top"),sQuery(id+"F2.wireOp",EDGE,"E19.left")])]})}),makeQuery(id+"F1.opExtrude","SWEPT_FACE",FACE,{"disambiguationData":[OSD([sQuery(id+"F0.wireOp",EDGE,"E11.top")])]})],"blendedInto":[makeQuery(id+"F1.opExtrude","SWEPT_FACE",FACE,{"disambiguationData":[OSD([sQuery(id+"F0.wireOp",EDGE,"E11.top")])]})]});
            var Q23;
            {var subQ0=sQuery(id+"F0.wireOp",EDGE,"E11.top");Q23=makeQuery(id+"F16.opFillet","BLEND_EDGE",EDGE,{"blendedFrom":[makeQuery(id+"F10.opFillet","BLEND_EDGE",EDGE,{"blendedFrom":[makeQuery(id+"F3.boolean.opBoolean","COPY",EDGE,{"derivedFrom":makeQuery(id+"F3.opExtrude","SWEPT_EDGE",EDGE,{"disambiguationData":[OSD([sQuery(id+"F2.wireOp",EDGE,"E19.top"),sQuery(id+"F2.wireOp",EDGE,"E19.left")])]})}),makeQuery(id+"F1.opExtrude","CAP_FACE",FACE,{"disambiguationData":[OSD([sQuery(id+"F0.wireOp",EDGE,"E0.top"),sQuery(id+"F0.wireOp",EDGE,"E1.top"),sQuery(id+"F0.wireOp",EDGE,"E1.right"),sQuery(id+"F0.wireOp",EDGE,"E2"),sQuery(id+"F0.wireOp",EDGE,"E3"),sQuery(id+"F0.wireOp",EDGE,"E4.top"),sQuery(id+"F0.wireOp",EDGE,"E4.right"),sQuery(id+"F0.wireOp",EDGE,"E6"),sQuery(id+"F0.wireOp",EDGE,"E7.MirrorCS"),sQuery(id+"F0.wireOp",EDGE,"E8"),sQuery(id+"F0.wireOp",EDGE,"E9.MirrorCS"),sQuery(id+"F0.wireOp",EDGE,"E10"),subQ0,sQuery(id+"F0.wireOp",EDGE,"E12.top"),sQuery(id+"F0.wireOp",EDGE,"E12.right"),sQuery(id+"F0.wireOp",EDGE,"E13"),sQuery(id+"F0.wireOp",EDGE,"E14"),sQuery(id+"F0.wireOp",EDGE,"E15"),sQuery(id+"F0.wireOp",EDGE,"E16"),sQuery(id+"F0.wireOp",EDGE,"E17")])],"isStart":true})],"blendedInto":[makeQuery(id+"F1.opExtrude","CAP_FACE",FACE,{"disambiguationData":[OSD([sQuery(id+"F0.wireOp",EDGE,"E0.top"),sQuery(id+"F0.wireOp",EDGE,"E1.top"),sQuery(id+"F0.wireOp",EDGE,"E1.right"),sQuery(id+"F0.wireOp",EDGE,"E2"),sQuery(id+"F0.wireOp",EDGE,"E3"),sQuery(id+"F0.wireOp",EDGE,"E4.top"),sQuery(id+"F0.wireOp",EDGE,"E4.right"),sQuery(id+"F0.wireOp",EDGE,"E6"),sQuery(id+"F0.wireOp",EDGE,"E7.MirrorCS"),sQuery(id+"F0.wireOp",EDGE,"E8"),sQuery(id+"F0.wireOp",EDGE,"E9.MirrorCS"),sQuery(id+"F0.wireOp",EDGE,"E10"),subQ0,sQuery(id+"F0.wireOp",EDGE,"E12.top"),sQuery(id+"F0.wireOp",EDGE,"E12.right"),sQuery(id+"F0.wireOp",EDGE,"E13"),sQuery(id+"F0.wireOp",EDGE,"E14"),sQuery(id+"F0.wireOp",EDGE,"E15"),sQuery(id+"F0.wireOp",EDGE,"E16"),sQuery(id+"F0.wireOp",EDGE,"E17")])],"isStart":true})]}),makeQuery(id+"F1.opExtrude","SWEPT_FACE",FACE,{"disambiguationData":[OSD([subQ0])]})],"blendedInto":[makeQuery(id+"F1.opExtrude","SWEPT_FACE",FACE,{"disambiguationData":[OSD([subQ0])]})]});}
            var Q24;
            Q24=makeQuery(id+"F1.opExtrude","CAP_EDGE",EDGE,{"disambiguationData":[OSD([sQuery(id+"F0.wireOp",EDGE,"E11.top")])],"isStart":true});
            var Q25;
            Q25=makeQuery(id+"F1.opExtrude","CAP_EDGE",EDGE,{"disambiguationData":[OSD([sQuery(id+"F0.wireOp",EDGE,"E15")])],"isStart":true});
            fillet(context, id + "F19", {"entities" : qUnion([Q0, Q1, Q2, Q3, Q4, Q5, Q6, Q7, Q8, Q9, Q10, Q11, Q12, Q13, Q14, Q15, Q16, Q17, Q18, Q19, Q20, Q21, Q22, Q23, Q24, Q25]), "radius" : 0.5 * mm, "tangentPropagation" : true, "rho" : 0.5, "crossSection" : FilletCrossSection.CONIC, "allowEdgeOverflow" : false});
        }
        {
            var Q0;
            Q0=makeQuery(id+"F1.opExtrude","CAP_EDGE",EDGE,{"disambiguationData":[OSD([sQuery(id+"F0.wireOp",EDGE,"E4.top")])],"isStart":false});
            var Q1;
            Q1=makeQuery(id+"F1.opExtrude","CAP_EDGE",EDGE,{"disambiguationData":[OSD([sQuery(id+"F0.wireOp",EDGE,"E6")])],"isStart":false});
            var Q2;
            Q2=makeQuery(id+"F1.opExtrude","CAP_EDGE",EDGE,{"disambiguationData":[OSD([sQuery(id+"F0.wireOp",EDGE,"E16")])],"isStart":false});
            var Q3;
            Q3=makeQuery(id+"F12.boolean.opBoolean","MERGE",EDGE,{"derivedFrom":[makeQuery(id+"F1.opExtrude","CAP_EDGE",EDGE,{"disambiguationData":[OSD([sQuery(id+"F0.wireOp",EDGE,"E4.right")])],"isStart":false}),makeQuery(id+"F12.opExtrude","CAP_EDGE",EDGE,{"disambiguationData":[OSD([sQuery(id+"F11.wireOp",EDGE,"E21.left")])],"isStart":true})]});
            var Q4;
            {var subQ0=sQuery(id+"F11.wireOp",EDGE,"E21.left");var subQ1=sQuery(id+"F11.wireOp",EDGE,"E21.top");Q4=makeQuery(id+"F13.opFillet","BLEND_EDGE",EDGE,{"blendedFrom":[makeQuery(id+"F12.opExtrude","SWEPT_EDGE",EDGE,{"disambiguationData":[OSD([subQ1,subQ0])]}),makeQuery(id+"F12.boolean.opBoolean","MERGE",FACE,{"derivedFrom":[makeQuery(id+"F1.opExtrude","CAP_FACE",FACE,{"disambiguationData":[OSD([sQuery(id+"F0.wireOp",EDGE,"E0.top"),sQuery(id+"F0.wireOp",EDGE,"E1.top"),sQuery(id+"F0.wireOp",EDGE,"E1.right"),sQuery(id+"F0.wireOp",EDGE,"E2"),sQuery(id+"F0.wireOp",EDGE,"E3"),sQuery(id+"F0.wireOp",EDGE,"E4.top"),sQuery(id+"F0.wireOp",EDGE,"E4.right"),sQuery(id+"F0.wireOp",EDGE,"E6"),sQuery(id+"F0.wireOp",EDGE,"E7.MirrorCS"),sQuery(id+"F0.wireOp",EDGE,"E8"),sQuery(id+"F0.wireOp",EDGE,"E9.MirrorCS"),sQuery(id+"F0.wireOp",EDGE,"E10"),sQuery(id+"F0.wireOp",EDGE,"E11.top"),sQuery(id+"F0.wireOp",EDGE,"E12.top"),sQuery(id+"F0.wireOp",EDGE,"E12.right"),sQuery(id+"F0.wireOp",EDGE,"E13"),sQuery(id+"F0.wireOp",EDGE,"E14"),sQuery(id+"F0.wireOp",EDGE,"E15"),sQuery(id+"F0.wireOp",EDGE,"E16"),sQuery(id+"F0.wireOp",EDGE,"E17")])],"isStart":false}),makeQuery(id+"F12.opExtrude","CAP_FACE",FACE,{"disambiguationData":[OSD([sQuery(id+"F11.wireOp",EDGE,"E21.bottom"),subQ1,subQ0,sQuery(id+"F11.wireOp",EDGE,"E21.right")])],"isStart":true})]})],"blendedInto":[makeQuery(id+"F12.boolean.opBoolean","MERGE",FACE,{"derivedFrom":[makeQuery(id+"F1.opExtrude","CAP_FACE",FACE,{"disambiguationData":[OSD([sQuery(id+"F0.wireOp",EDGE,"E0.top"),sQuery(id+"F0.wireOp",EDGE,"E1.top"),sQuery(id+"F0.wireOp",EDGE,"E1.right"),sQuery(id+"F0.wireOp",EDGE,"E2"),sQuery(id+"F0.wireOp",EDGE,"E3"),sQuery(id+"F0.wireOp",EDGE,"E4.top"),sQuery(id+"F0.wireOp",EDGE,"E4.right"),sQuery(id+"F0.wireOp",EDGE,"E6"),sQuery(id+"F0.wireOp",EDGE,"E7.MirrorCS"),sQuery(id+"F0.wireOp",EDGE,"E8"),sQuery(id+"F0.wireOp",EDGE,"E9.MirrorCS"),sQuery(id+"F0.wireOp",EDGE,"E10"),sQuery(id+"F0.wireOp",EDGE,"E11.top"),sQuery(id+"F0.wireOp",EDGE,"E12.top"),sQuery(id+"F0.wireOp",EDGE,"E12.right"),sQuery(id+"F0.wireOp",EDGE,"E13"),sQuery(id+"F0.wireOp",EDGE,"E14"),sQuery(id+"F0.wireOp",EDGE,"E15"),sQuery(id+"F0.wireOp",EDGE,"E16"),sQuery(id+"F0.wireOp",EDGE,"E17")])],"isStart":false}),makeQuery(id+"F12.opExtrude","CAP_FACE",FACE,{"disambiguationData":[OSD([sQuery(id+"F11.wireOp",EDGE,"E21.bottom"),subQ1,subQ0,sQuery(id+"F11.wireOp",EDGE,"E21.right")])],"isStart":true})]})]});}
            var Q5;
            Q5=makeQuery(id+"F12.opExtrude","CAP_EDGE",EDGE,{"disambiguationData":[OSD([sQuery(id+"F11.wireOp",EDGE,"E21.top")])],"isStart":true});
            var Q6;
            {var subQ0=sQuery(id+"F11.wireOp",EDGE,"E21.right");var subQ1=sQuery(id+"F11.wireOp",EDGE,"E21.top");Q6=makeQuery(id+"F13.opFillet","BLEND_EDGE",EDGE,{"blendedFrom":[makeQuery(id+"F12.opExtrude","SWEPT_EDGE",EDGE,{"disambiguationData":[OSD([subQ1,subQ0])]}),makeQuery(id+"F12.boolean.opBoolean","MERGE",FACE,{"derivedFrom":[makeQuery(id+"F1.opExtrude","CAP_FACE",FACE,{"disambiguationData":[OSD([sQuery(id+"F0.wireOp",EDGE,"E0.top"),sQuery(id+"F0.wireOp",EDGE,"E1.top"),sQuery(id+"F0.wireOp",EDGE,"E1.right"),sQuery(id+"F0.wireOp",EDGE,"E2"),sQuery(id+"F0.wireOp",EDGE,"E3"),sQuery(id+"F0.wireOp",EDGE,"E4.top"),sQuery(id+"F0.wireOp",EDGE,"E4.right"),sQuery(id+"F0.wireOp",EDGE,"E6"),sQuery(id+"F0.wireOp",EDGE,"E7.MirrorCS"),sQuery(id+"F0.wireOp",EDGE,"E8"),sQuery(id+"F0.wireOp",EDGE,"E9.MirrorCS"),sQuery(id+"F0.wireOp",EDGE,"E10"),sQuery(id+"F0.wireOp",EDGE,"E11.top"),sQuery(id+"F0.wireOp",EDGE,"E12.top"),sQuery(id+"F0.wireOp",EDGE,"E12.right"),sQuery(id+"F0.wireOp",EDGE,"E13"),sQuery(id+"F0.wireOp",EDGE,"E14"),sQuery(id+"F0.wireOp",EDGE,"E15"),sQuery(id+"F0.wireOp",EDGE,"E16"),sQuery(id+"F0.wireOp",EDGE,"E17")])],"isStart":false}),makeQuery(id+"F12.opExtrude","CAP_FACE",FACE,{"disambiguationData":[OSD([sQuery(id+"F11.wireOp",EDGE,"E21.bottom"),subQ1,sQuery(id+"F11.wireOp",EDGE,"E21.left"),subQ0])],"isStart":true})]})],"blendedInto":[makeQuery(id+"F12.boolean.opBoolean","MERGE",FACE,{"derivedFrom":[makeQuery(id+"F1.opExtrude","CAP_FACE",FACE,{"disambiguationData":[OSD([sQuery(id+"F0.wireOp",EDGE,"E0.top"),sQuery(id+"F0.wireOp",EDGE,"E1.top"),sQuery(id+"F0.wireOp",EDGE,"E1.right"),sQuery(id+"F0.wireOp",EDGE,"E2"),sQuery(id+"F0.wireOp",EDGE,"E3"),sQuery(id+"F0.wireOp",EDGE,"E4.top"),sQuery(id+"F0.wireOp",EDGE,"E4.right"),sQuery(id+"F0.wireOp",EDGE,"E6"),sQuery(id+"F0.wireOp",EDGE,"E7.MirrorCS"),sQuery(id+"F0.wireOp",EDGE,"E8"),sQuery(id+"F0.wireOp",EDGE,"E9.MirrorCS"),sQuery(id+"F0.wireOp",EDGE,"E10"),sQuery(id+"F0.wireOp",EDGE,"E11.top"),sQuery(id+"F0.wireOp",EDGE,"E12.top"),sQuery(id+"F0.wireOp",EDGE,"E12.right"),sQuery(id+"F0.wireOp",EDGE,"E13"),sQuery(id+"F0.wireOp",EDGE,"E14"),sQuery(id+"F0.wireOp",EDGE,"E15"),sQuery(id+"F0.wireOp",EDGE,"E16"),sQuery(id+"F0.wireOp",EDGE,"E17")])],"isStart":false}),makeQuery(id+"F12.opExtrude","CAP_FACE",FACE,{"disambiguationData":[OSD([sQuery(id+"F11.wireOp",EDGE,"E21.bottom"),subQ1,sQuery(id+"F11.wireOp",EDGE,"E21.left"),subQ0])],"isStart":true})]})]});}
            var Q7;
            Q7=makeQuery(id+"F12.opExtrude","CAP_EDGE",EDGE,{"disambiguationData":[OSD([sQuery(id+"F11.wireOp",EDGE,"E21.right")])],"isStart":true});
            var Q8;
            {var subQ0=sQuery(id+"F11.wireOp",EDGE,"E21.right");var subQ1=sQuery(id+"F0.wireOp",EDGE,"E8");Q8=makeQuery(id+"F15.opFillet","BLEND_EDGE",EDGE,{"blendedFrom":[makeQuery(id+"F12.boolean.opBoolean","INTERSECT",EDGE,{"derivedFrom":[makeQuery(id+"F1.opExtrude","SWEPT_FACE",FACE,{"disambiguationData":[OSD([subQ1])]}),makeQuery(id+"F12.opExtrude","SWEPT_FACE",FACE,{"disambiguationData":[OSD([subQ0])]})]}),makeQuery(id+"F12.boolean.opBoolean","MERGE",FACE,{"derivedFrom":[makeQuery(id+"F1.opExtrude","CAP_FACE",FACE,{"disambiguationData":[OSD([sQuery(id+"F0.wireOp",EDGE,"E0.top"),sQuery(id+"F0.wireOp",EDGE,"E1.top"),sQuery(id+"F0.wireOp",EDGE,"E1.right"),sQuery(id+"F0.wireOp",EDGE,"E2"),sQuery(id+"F0.wireOp",EDGE,"E3"),sQuery(id+"F0.wireOp",EDGE,"E4.top"),sQuery(id+"F0.wireOp",EDGE,"E4.right"),sQuery(id+"F0.wireOp",EDGE,"E6"),sQuery(id+"F0.wireOp",EDGE,"E7.MirrorCS"),subQ1,sQuery(id+"F0.wireOp",EDGE,"E9.MirrorCS"),sQuery(id+"F0.wireOp",EDGE,"E10"),sQuery(id+"F0.wireOp",EDGE,"E11.top"),sQuery(id+"F0.wireOp",EDGE,"E12.top"),sQuery(id+"F0.wireOp",EDGE,"E12.right"),sQuery(id+"F0.wireOp",EDGE,"E13"),sQuery(id+"F0.wireOp",EDGE,"E14"),sQuery(id+"F0.wireOp",EDGE,"E15"),sQuery(id+"F0.wireOp",EDGE,"E16"),sQuery(id+"F0.wireOp",EDGE,"E17")])],"isStart":false}),makeQuery(id+"F12.opExtrude","CAP_FACE",FACE,{"disambiguationData":[OSD([sQuery(id+"F11.wireOp",EDGE,"E21.bottom"),sQuery(id+"F11.wireOp",EDGE,"E21.top"),sQuery(id+"F11.wireOp",EDGE,"E21.left"),subQ0])],"isStart":true})]})],"blendedInto":[makeQuery(id+"F12.boolean.opBoolean","MERGE",FACE,{"derivedFrom":[makeQuery(id+"F1.opExtrude","CAP_FACE",FACE,{"disambiguationData":[OSD([sQuery(id+"F0.wireOp",EDGE,"E0.top"),sQuery(id+"F0.wireOp",EDGE,"E1.top"),sQuery(id+"F0.wireOp",EDGE,"E1.right"),sQuery(id+"F0.wireOp",EDGE,"E2"),sQuery(id+"F0.wireOp",EDGE,"E3"),sQuery(id+"F0.wireOp",EDGE,"E4.top"),sQuery(id+"F0.wireOp",EDGE,"E4.right"),sQuery(id+"F0.wireOp",EDGE,"E6"),sQuery(id+"F0.wireOp",EDGE,"E7.MirrorCS"),subQ1,sQuery(id+"F0.wireOp",EDGE,"E9.MirrorCS"),sQuery(id+"F0.wireOp",EDGE,"E10"),sQuery(id+"F0.wireOp",EDGE,"E11.top"),sQuery(id+"F0.wireOp",EDGE,"E12.top"),sQuery(id+"F0.wireOp",EDGE,"E12.right"),sQuery(id+"F0.wireOp",EDGE,"E13"),sQuery(id+"F0.wireOp",EDGE,"E14"),sQuery(id+"F0.wireOp",EDGE,"E15"),sQuery(id+"F0.wireOp",EDGE,"E16"),sQuery(id+"F0.wireOp",EDGE,"E17")])],"isStart":false}),makeQuery(id+"F12.opExtrude","CAP_FACE",FACE,{"disambiguationData":[OSD([sQuery(id+"F11.wireOp",EDGE,"E21.bottom"),sQuery(id+"F11.wireOp",EDGE,"E21.top"),sQuery(id+"F11.wireOp",EDGE,"E21.left"),subQ0])],"isStart":true})]})]});}
            var Q9;
            {var subQ0=sQuery(id+"F0.wireOp",EDGE,"E9.MirrorCS");var subQ1=sQuery(id+"F0.wireOp",EDGE,"E8");Q9=makeQuery(id+"F8.opFillet","BLEND_EDGE",EDGE,{"blendedFrom":[makeQuery(id+"F1.opExtrude","SWEPT_EDGE",EDGE,{"disambiguationData":[OSD([subQ1,subQ0])]}),makeQuery(id+"F1.opExtrude","CAP_FACE",FACE,{"disambiguationData":[OSD([sQuery(id+"F0.wireOp",EDGE,"E0.top"),sQuery(id+"F0.wireOp",EDGE,"E1.top"),sQuery(id+"F0.wireOp",EDGE,"E1.right"),sQuery(id+"F0.wireOp",EDGE,"E2"),sQuery(id+"F0.wireOp",EDGE,"E3"),sQuery(id+"F0.wireOp",EDGE,"E4.top"),sQuery(id+"F0.wireOp",EDGE,"E4.right"),sQuery(id+"F0.wireOp",EDGE,"E6"),sQuery(id+"F0.wireOp",EDGE,"E7.MirrorCS"),subQ1,subQ0,sQuery(id+"F0.wireOp",EDGE,"E10"),sQuery(id+"F0.wireOp",EDGE,"E11.top"),sQuery(id+"F0.wireOp",EDGE,"E12.top"),sQuery(id+"F0.wireOp",EDGE,"E12.right"),sQuery(id+"F0.wireOp",EDGE,"E13"),sQuery(id+"F0.wireOp",EDGE,"E14"),sQuery(id+"F0.wireOp",EDGE,"E15"),sQuery(id+"F0.wireOp",EDGE,"E16"),sQuery(id+"F0.wireOp",EDGE,"E17")])],"isStart":false})],"blendedInto":[makeQuery(id+"F1.opExtrude","CAP_FACE",FACE,{"disambiguationData":[OSD([sQuery(id+"F0.wireOp",EDGE,"E0.top"),sQuery(id+"F0.wireOp",EDGE,"E1.top"),sQuery(id+"F0.wireOp",EDGE,"E1.right"),sQuery(id+"F0.wireOp",EDGE,"E2"),sQuery(id+"F0.wireOp",EDGE,"E3"),sQuery(id+"F0.wireOp",EDGE,"E4.top"),sQuery(id+"F0.wireOp",EDGE,"E4.right"),sQuery(id+"F0.wireOp",EDGE,"E6"),sQuery(id+"F0.wireOp",EDGE,"E7.MirrorCS"),subQ1,subQ0,sQuery(id+"F0.wireOp",EDGE,"E10"),sQuery(id+"F0.wireOp",EDGE,"E11.top"),sQuery(id+"F0.wireOp",EDGE,"E12.top"),sQuery(id+"F0.wireOp",EDGE,"E12.right"),sQuery(id+"F0.wireOp",EDGE,"E13"),sQuery(id+"F0.wireOp",EDGE,"E14"),sQuery(id+"F0.wireOp",EDGE,"E15"),sQuery(id+"F0.wireOp",EDGE,"E16"),sQuery(id+"F0.wireOp",EDGE,"E17")])],"isStart":false})]});}
            var Q10;
            {var subQ0=sQuery(id+"F0.wireOp",EDGE,"E7.MirrorCS");var subQ1=sQuery(id+"F0.wireOp",EDGE,"E6");Q10=makeQuery(id+"F7.opFillet","BLEND_EDGE",EDGE,{"blendedFrom":[makeQuery(id+"F1.opExtrude","SWEPT_EDGE",EDGE,{"disambiguationData":[OSD([subQ1,subQ0])]}),makeQuery(id+"F1.opExtrude","CAP_FACE",FACE,{"disambiguationData":[OSD([sQuery(id+"F0.wireOp",EDGE,"E0.top"),sQuery(id+"F0.wireOp",EDGE,"E1.top"),sQuery(id+"F0.wireOp",EDGE,"E1.right"),sQuery(id+"F0.wireOp",EDGE,"E2"),sQuery(id+"F0.wireOp",EDGE,"E3"),sQuery(id+"F0.wireOp",EDGE,"E4.top"),sQuery(id+"F0.wireOp",EDGE,"E4.right"),subQ1,subQ0,sQuery(id+"F0.wireOp",EDGE,"E8"),sQuery(id+"F0.wireOp",EDGE,"E9.MirrorCS"),sQuery(id+"F0.wireOp",EDGE,"E10"),sQuery(id+"F0.wireOp",EDGE,"E11.top"),sQuery(id+"F0.wireOp",EDGE,"E12.top"),sQuery(id+"F0.wireOp",EDGE,"E12.right"),sQuery(id+"F0.wireOp",EDGE,"E13"),sQuery(id+"F0.wireOp",EDGE,"E14"),sQuery(id+"F0.wireOp",EDGE,"E15"),sQuery(id+"F0.wireOp",EDGE,"E16"),sQuery(id+"F0.wireOp",EDGE,"E17")])],"isStart":false})],"blendedInto":[makeQuery(id+"F1.opExtrude","CAP_FACE",FACE,{"disambiguationData":[OSD([sQuery(id+"F0.wireOp",EDGE,"E0.top"),sQuery(id+"F0.wireOp",EDGE,"E1.top"),sQuery(id+"F0.wireOp",EDGE,"E1.right"),sQuery(id+"F0.wireOp",EDGE,"E2"),sQuery(id+"F0.wireOp",EDGE,"E3"),sQuery(id+"F0.wireOp",EDGE,"E4.top"),sQuery(id+"F0.wireOp",EDGE,"E4.right"),subQ1,subQ0,sQuery(id+"F0.wireOp",EDGE,"E8"),sQuery(id+"F0.wireOp",EDGE,"E9.MirrorCS"),sQuery(id+"F0.wireOp",EDGE,"E10"),sQuery(id+"F0.wireOp",EDGE,"E11.top"),sQuery(id+"F0.wireOp",EDGE,"E12.top"),sQuery(id+"F0.wireOp",EDGE,"E12.right"),sQuery(id+"F0.wireOp",EDGE,"E13"),sQuery(id+"F0.wireOp",EDGE,"E14"),sQuery(id+"F0.wireOp",EDGE,"E15"),sQuery(id+"F0.wireOp",EDGE,"E16"),sQuery(id+"F0.wireOp",EDGE,"E17")])],"isStart":false})]});}
            var Q11;
            Q11=makeQuery(id+"F1.opExtrude","CAP_EDGE",EDGE,{"disambiguationData":[OSD([sQuery(id+"F0.wireOp",EDGE,"E7.MirrorCS")])],"isStart":false});
            var Q12;
            Q12=makeQuery(id+"F1.opExtrude","CAP_EDGE",EDGE,{"disambiguationData":[OSD([sQuery(id+"F0.wireOp",EDGE,"E9.MirrorCS")])],"isStart":false});
            var Q13;
            Q13=makeQuery(id+"F1.opExtrude","CAP_EDGE",EDGE,{"disambiguationData":[OSD([sQuery(id+"F0.wireOp",EDGE,"E10")])],"isStart":false});
            var Q14;
            {var subQ0=sQuery(id+"F0.wireOp",EDGE,"E10");var subQ1=sQuery(id+"F0.wireOp",EDGE,"E0.top");Q14=makeQuery(id+"F4.opFillet","BLEND_EDGE",EDGE,{"blendedFrom":[makeQuery(id+"F1.opExtrude","SWEPT_EDGE",EDGE,{"disambiguationData":[OSD([subQ1,subQ0])]}),makeQuery(id+"F1.opExtrude","CAP_FACE",FACE,{"disambiguationData":[OSD([subQ1,sQuery(id+"F0.wireOp",EDGE,"E1.top"),sQuery(id+"F0.wireOp",EDGE,"E1.right"),sQuery(id+"F0.wireOp",EDGE,"E2"),sQuery(id+"F0.wireOp",EDGE,"E3"),sQuery(id+"F0.wireOp",EDGE,"E4.top"),sQuery(id+"F0.wireOp",EDGE,"E4.right"),sQuery(id+"F0.wireOp",EDGE,"E6"),sQuery(id+"F0.wireOp",EDGE,"E7.MirrorCS"),sQuery(id+"F0.wireOp",EDGE,"E8"),sQuery(id+"F0.wireOp",EDGE,"E9.MirrorCS"),subQ0,sQuery(id+"F0.wireOp",EDGE,"E11.top"),sQuery(id+"F0.wireOp",EDGE,"E12.top"),sQuery(id+"F0.wireOp",EDGE,"E12.right"),sQuery(id+"F0.wireOp",EDGE,"E13"),sQuery(id+"F0.wireOp",EDGE,"E14"),sQuery(id+"F0.wireOp",EDGE,"E15"),sQuery(id+"F0.wireOp",EDGE,"E16"),sQuery(id+"F0.wireOp",EDGE,"E17")])],"isStart":false})],"blendedInto":[makeQuery(id+"F1.opExtrude","CAP_FACE",FACE,{"disambiguationData":[OSD([subQ1,sQuery(id+"F0.wireOp",EDGE,"E1.top"),sQuery(id+"F0.wireOp",EDGE,"E1.right"),sQuery(id+"F0.wireOp",EDGE,"E2"),sQuery(id+"F0.wireOp",EDGE,"E3"),sQuery(id+"F0.wireOp",EDGE,"E4.top"),sQuery(id+"F0.wireOp",EDGE,"E4.right"),sQuery(id+"F0.wireOp",EDGE,"E6"),sQuery(id+"F0.wireOp",EDGE,"E7.MirrorCS"),sQuery(id+"F0.wireOp",EDGE,"E8"),sQuery(id+"F0.wireOp",EDGE,"E9.MirrorCS"),subQ0,sQuery(id+"F0.wireOp",EDGE,"E11.top"),sQuery(id+"F0.wireOp",EDGE,"E12.top"),sQuery(id+"F0.wireOp",EDGE,"E12.right"),sQuery(id+"F0.wireOp",EDGE,"E13"),sQuery(id+"F0.wireOp",EDGE,"E14"),sQuery(id+"F0.wireOp",EDGE,"E15"),sQuery(id+"F0.wireOp",EDGE,"E16"),sQuery(id+"F0.wireOp",EDGE,"E17")])],"isStart":false})]});}
            var Q15;
            Q15=makeQuery(id+"F1.opExtrude","CAP_EDGE",EDGE,{"disambiguationData":[OSD([sQuery(id+"F0.wireOp",EDGE,"E0.top")])],"isStart":false});
            var Q16;
            {var subQ0=sQuery(id+"F0.wireOp",EDGE,"E1.right");var subQ1=sQuery(id+"F0.wireOp",EDGE,"E0.top");Q16=makeQuery(id+"F4.opFillet","BLEND_EDGE",EDGE,{"blendedFrom":[makeQuery(id+"F1.opExtrude","SWEPT_EDGE",EDGE,{"disambiguationData":[OSD([subQ1,subQ0])]}),makeQuery(id+"F1.opExtrude","CAP_FACE",FACE,{"disambiguationData":[OSD([subQ1,sQuery(id+"F0.wireOp",EDGE,"E1.top"),subQ0,sQuery(id+"F0.wireOp",EDGE,"E2"),sQuery(id+"F0.wireOp",EDGE,"E3"),sQuery(id+"F0.wireOp",EDGE,"E4.top"),sQuery(id+"F0.wireOp",EDGE,"E4.right"),sQuery(id+"F0.wireOp",EDGE,"E6"),sQuery(id+"F0.wireOp",EDGE,"E7.MirrorCS"),sQuery(id+"F0.wireOp",EDGE,"E8"),sQuery(id+"F0.wireOp",EDGE,"E9.MirrorCS"),sQuery(id+"F0.wireOp",EDGE,"E10"),sQuery(id+"F0.wireOp",EDGE,"E11.top"),sQuery(id+"F0.wireOp",EDGE,"E12.top"),sQuery(id+"F0.wireOp",EDGE,"E12.right"),sQuery(id+"F0.wireOp",EDGE,"E13"),sQuery(id+"F0.wireOp",EDGE,"E14"),sQuery(id+"F0.wireOp",EDGE,"E15"),sQuery(id+"F0.wireOp",EDGE,"E16"),sQuery(id+"F0.wireOp",EDGE,"E17")])],"isStart":false})],"blendedInto":[makeQuery(id+"F1.opExtrude","CAP_FACE",FACE,{"disambiguationData":[OSD([subQ1,sQuery(id+"F0.wireOp",EDGE,"E1.top"),subQ0,sQuery(id+"F0.wireOp",EDGE,"E2"),sQuery(id+"F0.wireOp",EDGE,"E3"),sQuery(id+"F0.wireOp",EDGE,"E4.top"),sQuery(id+"F0.wireOp",EDGE,"E4.right"),sQuery(id+"F0.wireOp",EDGE,"E6"),sQuery(id+"F0.wireOp",EDGE,"E7.MirrorCS"),sQuery(id+"F0.wireOp",EDGE,"E8"),sQuery(id+"F0.wireOp",EDGE,"E9.MirrorCS"),sQuery(id+"F0.wireOp",EDGE,"E10"),sQuery(id+"F0.wireOp",EDGE,"E11.top"),sQuery(id+"F0.wireOp",EDGE,"E12.top"),sQuery(id+"F0.wireOp",EDGE,"E12.right"),sQuery(id+"F0.wireOp",EDGE,"E13"),sQuery(id+"F0.wireOp",EDGE,"E14"),sQuery(id+"F0.wireOp",EDGE,"E15"),sQuery(id+"F0.wireOp",EDGE,"E16"),sQuery(id+"F0.wireOp",EDGE,"E17")])],"isStart":false})]});}
            var Q17;
            {var subQ0=sQuery(id+"F0.wireOp",EDGE,"E1.right");var subQ1=sQuery(id+"F0.wireOp",EDGE,"E1.top");var subQ2=sQuery(id+"F0.wireOp",EDGE,"E0.top");Q17=makeQuery(id+"F5.opFillet","BLEND_EDGE",EDGE,{"blendedFrom":[makeQuery(id+"F4.opFillet","BLEND_EDGE",EDGE,{"blendedFrom":[makeQuery(id+"F1.opExtrude","SWEPT_EDGE",EDGE,{"disambiguationData":[OSD([subQ2,subQ0])]}),makeQuery(id+"F1.opExtrude","SWEPT_FACE",FACE,{"disambiguationData":[OSD([subQ1])]})],"blendedInto":[makeQuery(id+"F1.opExtrude","SWEPT_FACE",FACE,{"disambiguationData":[OSD([subQ1])]})]}),makeQuery(id+"F1.opExtrude","CAP_FACE",FACE,{"disambiguationData":[OSD([subQ2,subQ1,subQ0,sQuery(id+"F0.wireOp",EDGE,"E2"),sQuery(id+"F0.wireOp",EDGE,"E3"),sQuery(id+"F0.wireOp",EDGE,"E4.top"),sQuery(id+"F0.wireOp",EDGE,"E4.right"),sQuery(id+"F0.wireOp",EDGE,"E6"),sQuery(id+"F0.wireOp",EDGE,"E7.MirrorCS"),sQuery(id+"F0.wireOp",EDGE,"E8"),sQuery(id+"F0.wireOp",EDGE,"E9.MirrorCS"),sQuery(id+"F0.wireOp",EDGE,"E10"),sQuery(id+"F0.wireOp",EDGE,"E11.top"),sQuery(id+"F0.wireOp",EDGE,"E12.top"),sQuery(id+"F0.wireOp",EDGE,"E12.right"),sQuery(id+"F0.wireOp",EDGE,"E13"),sQuery(id+"F0.wireOp",EDGE,"E14"),sQuery(id+"F0.wireOp",EDGE,"E15"),sQuery(id+"F0.wireOp",EDGE,"E16"),sQuery(id+"F0.wireOp",EDGE,"E17")])],"isStart":false})],"blendedInto":[makeQuery(id+"F1.opExtrude","CAP_FACE",FACE,{"disambiguationData":[OSD([subQ2,subQ1,subQ0,sQuery(id+"F0.wireOp",EDGE,"E2"),sQuery(id+"F0.wireOp",EDGE,"E3"),sQuery(id+"F0.wireOp",EDGE,"E4.top"),sQuery(id+"F0.wireOp",EDGE,"E4.right"),sQuery(id+"F0.wireOp",EDGE,"E6"),sQuery(id+"F0.wireOp",EDGE,"E7.MirrorCS"),sQuery(id+"F0.wireOp",EDGE,"E8"),sQuery(id+"F0.wireOp",EDGE,"E9.MirrorCS"),sQuery(id+"F0.wireOp",EDGE,"E10"),sQuery(id+"F0.wireOp",EDGE,"E11.top"),sQuery(id+"F0.wireOp",EDGE,"E12.top"),sQuery(id+"F0.wireOp",EDGE,"E12.right"),sQuery(id+"F0.wireOp",EDGE,"E13"),sQuery(id+"F0.wireOp",EDGE,"E14"),sQuery(id+"F0.wireOp",EDGE,"E15"),sQuery(id+"F0.wireOp",EDGE,"E16"),sQuery(id+"F0.wireOp",EDGE,"E17")])],"isStart":false})]});}
            var Q18;
            Q18=makeQuery(id+"F1.opExtrude","CAP_EDGE",EDGE,{"disambiguationData":[OSD([sQuery(id+"F0.wireOp",EDGE,"E1.top")])],"isStart":false});
            var Q19;
            {var subQ0=sQuery(id+"F0.wireOp",EDGE,"E2");var subQ1=sQuery(id+"F0.wireOp",EDGE,"E1.top");Q19=makeQuery(id+"F5.opFillet","BLEND_EDGE",EDGE,{"blendedFrom":[makeQuery(id+"F1.opExtrude","SWEPT_EDGE",EDGE,{"disambiguationData":[OSD([subQ1,subQ0])]}),makeQuery(id+"F1.opExtrude","CAP_FACE",FACE,{"disambiguationData":[OSD([sQuery(id+"F0.wireOp",EDGE,"E0.top"),subQ1,sQuery(id+"F0.wireOp",EDGE,"E1.right"),subQ0,sQuery(id+"F0.wireOp",EDGE,"E3"),sQuery(id+"F0.wireOp",EDGE,"E4.top"),sQuery(id+"F0.wireOp",EDGE,"E4.right"),sQuery(id+"F0.wireOp",EDGE,"E6"),sQuery(id+"F0.wireOp",EDGE,"E7.MirrorCS"),sQuery(id+"F0.wireOp",EDGE,"E8"),sQuery(id+"F0.wireOp",EDGE,"E9.MirrorCS"),sQuery(id+"F0.wireOp",EDGE,"E10"),sQuery(id+"F0.wireOp",EDGE,"E11.top"),sQuery(id+"F0.wireOp",EDGE,"E12.top"),sQuery(id+"F0.wireOp",EDGE,"E12.right"),sQuery(id+"F0.wireOp",EDGE,"E13"),sQuery(id+"F0.wireOp",EDGE,"E14"),sQuery(id+"F0.wireOp",EDGE,"E15"),sQuery(id+"F0.wireOp",EDGE,"E16"),sQuery(id+"F0.wireOp",EDGE,"E17")])],"isStart":false})],"blendedInto":[makeQuery(id+"F1.opExtrude","CAP_FACE",FACE,{"disambiguationData":[OSD([sQuery(id+"F0.wireOp",EDGE,"E0.top"),subQ1,sQuery(id+"F0.wireOp",EDGE,"E1.right"),subQ0,sQuery(id+"F0.wireOp",EDGE,"E3"),sQuery(id+"F0.wireOp",EDGE,"E4.top"),sQuery(id+"F0.wireOp",EDGE,"E4.right"),sQuery(id+"F0.wireOp",EDGE,"E6"),sQuery(id+"F0.wireOp",EDGE,"E7.MirrorCS"),sQuery(id+"F0.wireOp",EDGE,"E8"),sQuery(id+"F0.wireOp",EDGE,"E9.MirrorCS"),sQuery(id+"F0.wireOp",EDGE,"E10"),sQuery(id+"F0.wireOp",EDGE,"E11.top"),sQuery(id+"F0.wireOp",EDGE,"E12.top"),sQuery(id+"F0.wireOp",EDGE,"E12.right"),sQuery(id+"F0.wireOp",EDGE,"E13"),sQuery(id+"F0.wireOp",EDGE,"E14"),sQuery(id+"F0.wireOp",EDGE,"E15"),sQuery(id+"F0.wireOp",EDGE,"E16"),sQuery(id+"F0.wireOp",EDGE,"E17")])],"isStart":false})]});}
            var Q20;
            {var subQ0=sQuery(id+"F0.wireOp",EDGE,"E3");var subQ1=sQuery(id+"F0.wireOp",EDGE,"E2");Q20=makeQuery(id+"F6.opFillet","BLEND_EDGE",EDGE,{"blendedFrom":[makeQuery(id+"F1.opExtrude","SWEPT_EDGE",EDGE,{"disambiguationData":[OSD([subQ1,subQ0])]}),makeQuery(id+"F1.opExtrude","CAP_FACE",FACE,{"disambiguationData":[OSD([sQuery(id+"F0.wireOp",EDGE,"E0.top"),sQuery(id+"F0.wireOp",EDGE,"E1.top"),sQuery(id+"F0.wireOp",EDGE,"E1.right"),subQ1,subQ0,sQuery(id+"F0.wireOp",EDGE,"E4.top"),sQuery(id+"F0.wireOp",EDGE,"E4.right"),sQuery(id+"F0.wireOp",EDGE,"E6"),sQuery(id+"F0.wireOp",EDGE,"E7.MirrorCS"),sQuery(id+"F0.wireOp",EDGE,"E8"),sQuery(id+"F0.wireOp",EDGE,"E9.MirrorCS"),sQuery(id+"F0.wireOp",EDGE,"E10"),sQuery(id+"F0.wireOp",EDGE,"E11.top"),sQuery(id+"F0.wireOp",EDGE,"E12.top"),sQuery(id+"F0.wireOp",EDGE,"E12.right"),sQuery(id+"F0.wireOp",EDGE,"E13"),sQuery(id+"F0.wireOp",EDGE,"E14"),sQuery(id+"F0.wireOp",EDGE,"E15"),sQuery(id+"F0.wireOp",EDGE,"E16"),sQuery(id+"F0.wireOp",EDGE,"E17")])],"isStart":false})],"blendedInto":[makeQuery(id+"F1.opExtrude","CAP_FACE",FACE,{"disambiguationData":[OSD([sQuery(id+"F0.wireOp",EDGE,"E0.top"),sQuery(id+"F0.wireOp",EDGE,"E1.top"),sQuery(id+"F0.wireOp",EDGE,"E1.right"),subQ1,subQ0,sQuery(id+"F0.wireOp",EDGE,"E4.top"),sQuery(id+"F0.wireOp",EDGE,"E4.right"),sQuery(id+"F0.wireOp",EDGE,"E6"),sQuery(id+"F0.wireOp",EDGE,"E7.MirrorCS"),sQuery(id+"F0.wireOp",EDGE,"E8"),sQuery(id+"F0.wireOp",EDGE,"E9.MirrorCS"),sQuery(id+"F0.wireOp",EDGE,"E10"),sQuery(id+"F0.wireOp",EDGE,"E11.top"),sQuery(id+"F0.wireOp",EDGE,"E12.top"),sQuery(id+"F0.wireOp",EDGE,"E12.right"),sQuery(id+"F0.wireOp",EDGE,"E13"),sQuery(id+"F0.wireOp",EDGE,"E14"),sQuery(id+"F0.wireOp",EDGE,"E15"),sQuery(id+"F0.wireOp",EDGE,"E16"),sQuery(id+"F0.wireOp",EDGE,"E17")])],"isStart":false})]});}
            var Q21;
            Q21=makeQuery(id+"F1.opExtrude","CAP_EDGE",EDGE,{"disambiguationData":[OSD([sQuery(id+"F0.wireOp",EDGE,"E3")])],"isStart":false});
            var Q22;
            {var subQ0=sQuery(id+"F0.wireOp",EDGE,"E15");var subQ1=sQuery(id+"F0.wireOp",EDGE,"E3");Q22=makeQuery(id+"F4.opFillet","BLEND_EDGE",EDGE,{"blendedFrom":[makeQuery(id+"F1.opExtrude","SWEPT_EDGE",EDGE,{"disambiguationData":[OSD([subQ1,subQ0])]}),makeQuery(id+"F1.opExtrude","CAP_FACE",FACE,{"disambiguationData":[OSD([sQuery(id+"F0.wireOp",EDGE,"E0.top"),sQuery(id+"F0.wireOp",EDGE,"E1.top"),sQuery(id+"F0.wireOp",EDGE,"E1.right"),sQuery(id+"F0.wireOp",EDGE,"E2"),subQ1,sQuery(id+"F0.wireOp",EDGE,"E4.top"),sQuery(id+"F0.wireOp",EDGE,"E4.right"),sQuery(id+"F0.wireOp",EDGE,"E6"),sQuery(id+"F0.wireOp",EDGE,"E7.MirrorCS"),sQuery(id+"F0.wireOp",EDGE,"E8"),sQuery(id+"F0.wireOp",EDGE,"E9.MirrorCS"),sQuery(id+"F0.wireOp",EDGE,"E10"),sQuery(id+"F0.wireOp",EDGE,"E11.top"),sQuery(id+"F0.wireOp",EDGE,"E12.top"),sQuery(id+"F0.wireOp",EDGE,"E12.right"),sQuery(id+"F0.wireOp",EDGE,"E13"),sQuery(id+"F0.wireOp",EDGE,"E14"),subQ0,sQuery(id+"F0.wireOp",EDGE,"E16"),sQuery(id+"F0.wireOp",EDGE,"E17")])],"isStart":false})],"blendedInto":[makeQuery(id+"F1.opExtrude","CAP_FACE",FACE,{"disambiguationData":[OSD([sQuery(id+"F0.wireOp",EDGE,"E0.top"),sQuery(id+"F0.wireOp",EDGE,"E1.top"),sQuery(id+"F0.wireOp",EDGE,"E1.right"),sQuery(id+"F0.wireOp",EDGE,"E2"),subQ1,sQuery(id+"F0.wireOp",EDGE,"E4.top"),sQuery(id+"F0.wireOp",EDGE,"E4.right"),sQuery(id+"F0.wireOp",EDGE,"E6"),sQuery(id+"F0.wireOp",EDGE,"E7.MirrorCS"),sQuery(id+"F0.wireOp",EDGE,"E8"),sQuery(id+"F0.wireOp",EDGE,"E9.MirrorCS"),sQuery(id+"F0.wireOp",EDGE,"E10"),sQuery(id+"F0.wireOp",EDGE,"E11.top"),sQuery(id+"F0.wireOp",EDGE,"E12.top"),sQuery(id+"F0.wireOp",EDGE,"E12.right"),sQuery(id+"F0.wireOp",EDGE,"E13"),sQuery(id+"F0.wireOp",EDGE,"E14"),subQ0,sQuery(id+"F0.wireOp",EDGE,"E16"),sQuery(id+"F0.wireOp",EDGE,"E17")])],"isStart":false})]});}
            var Q23;
            Q23=makeQuery(id+"F1.opExtrude","CAP_EDGE",EDGE,{"disambiguationData":[OSD([sQuery(id+"F0.wireOp",EDGE,"E11.top")])],"isStart":false});
            var Q24;
            {var subQ0=sQuery(id+"F0.wireOp",EDGE,"E12.right");var subQ1=sQuery(id+"F0.wireOp",EDGE,"E11.top");Q24=makeQuery(id+"F4.opFillet","BLEND_EDGE",EDGE,{"blendedFrom":[makeQuery(id+"F1.opExtrude","SWEPT_EDGE",EDGE,{"disambiguationData":[OSD([subQ1,subQ0])]}),makeQuery(id+"F1.opExtrude","CAP_FACE",FACE,{"disambiguationData":[OSD([sQuery(id+"F0.wireOp",EDGE,"E0.top"),sQuery(id+"F0.wireOp",EDGE,"E1.top"),sQuery(id+"F0.wireOp",EDGE,"E1.right"),sQuery(id+"F0.wireOp",EDGE,"E2"),sQuery(id+"F0.wireOp",EDGE,"E3"),sQuery(id+"F0.wireOp",EDGE,"E4.top"),sQuery(id+"F0.wireOp",EDGE,"E4.right"),sQuery(id+"F0.wireOp",EDGE,"E6"),sQuery(id+"F0.wireOp",EDGE,"E7.MirrorCS"),sQuery(id+"F0.wireOp",EDGE,"E8"),sQuery(id+"F0.wireOp",EDGE,"E9.MirrorCS"),sQuery(id+"F0.wireOp",EDGE,"E10"),subQ1,sQuery(id+"F0.wireOp",EDGE,"E12.top"),subQ0,sQuery(id+"F0.wireOp",EDGE,"E13"),sQuery(id+"F0.wireOp",EDGE,"E14"),sQuery(id+"F0.wireOp",EDGE,"E15"),sQuery(id+"F0.wireOp",EDGE,"E16"),sQuery(id+"F0.wireOp",EDGE,"E17")])],"isStart":false})],"blendedInto":[makeQuery(id+"F1.opExtrude","CAP_FACE",FACE,{"disambiguationData":[OSD([sQuery(id+"F0.wireOp",EDGE,"E0.top"),sQuery(id+"F0.wireOp",EDGE,"E1.top"),sQuery(id+"F0.wireOp",EDGE,"E1.right"),sQuery(id+"F0.wireOp",EDGE,"E2"),sQuery(id+"F0.wireOp",EDGE,"E3"),sQuery(id+"F0.wireOp",EDGE,"E4.top"),sQuery(id+"F0.wireOp",EDGE,"E4.right"),sQuery(id+"F0.wireOp",EDGE,"E6"),sQuery(id+"F0.wireOp",EDGE,"E7.MirrorCS"),sQuery(id+"F0.wireOp",EDGE,"E8"),sQuery(id+"F0.wireOp",EDGE,"E9.MirrorCS"),sQuery(id+"F0.wireOp",EDGE,"E10"),subQ1,sQuery(id+"F0.wireOp",EDGE,"E12.top"),subQ0,sQuery(id+"F0.wireOp",EDGE,"E13"),sQuery(id+"F0.wireOp",EDGE,"E14"),sQuery(id+"F0.wireOp",EDGE,"E15"),sQuery(id+"F0.wireOp",EDGE,"E16"),sQuery(id+"F0.wireOp",EDGE,"E17")])],"isStart":false})]});}
            var Q25;
            {var subQ0=sQuery(id+"F0.wireOp",EDGE,"E12.right");var subQ1=sQuery(id+"F0.wireOp",EDGE,"E12.top");var subQ2=sQuery(id+"F0.wireOp",EDGE,"E11.top");Q25=makeQuery(id+"F5.opFillet","BLEND_EDGE",EDGE,{"blendedFrom":[makeQuery(id+"F4.opFillet","BLEND_EDGE",EDGE,{"blendedFrom":[makeQuery(id+"F1.opExtrude","SWEPT_EDGE",EDGE,{"disambiguationData":[OSD([subQ2,subQ0])]}),makeQuery(id+"F1.opExtrude","SWEPT_FACE",FACE,{"disambiguationData":[OSD([subQ1])]})],"blendedInto":[makeQuery(id+"F1.opExtrude","SWEPT_FACE",FACE,{"disambiguationData":[OSD([subQ1])]})]}),makeQuery(id+"F1.opExtrude","CAP_FACE",FACE,{"disambiguationData":[OSD([sQuery(id+"F0.wireOp",EDGE,"E0.top"),sQuery(id+"F0.wireOp",EDGE,"E1.top"),sQuery(id+"F0.wireOp",EDGE,"E1.right"),sQuery(id+"F0.wireOp",EDGE,"E2"),sQuery(id+"F0.wireOp",EDGE,"E3"),sQuery(id+"F0.wireOp",EDGE,"E4.top"),sQuery(id+"F0.wireOp",EDGE,"E4.right"),sQuery(id+"F0.wireOp",EDGE,"E6"),sQuery(id+"F0.wireOp",EDGE,"E7.MirrorCS"),sQuery(id+"F0.wireOp",EDGE,"E8"),sQuery(id+"F0.wireOp",EDGE,"E9.MirrorCS"),sQuery(id+"F0.wireOp",EDGE,"E10"),subQ2,subQ1,subQ0,sQuery(id+"F0.wireOp",EDGE,"E13"),sQuery(id+"F0.wireOp",EDGE,"E14"),sQuery(id+"F0.wireOp",EDGE,"E15"),sQuery(id+"F0.wireOp",EDGE,"E16"),sQuery(id+"F0.wireOp",EDGE,"E17")])],"isStart":false})],"blendedInto":[makeQuery(id+"F1.opExtrude","CAP_FACE",FACE,{"disambiguationData":[OSD([sQuery(id+"F0.wireOp",EDGE,"E0.top"),sQuery(id+"F0.wireOp",EDGE,"E1.top"),sQuery(id+"F0.wireOp",EDGE,"E1.right"),sQuery(id+"F0.wireOp",EDGE,"E2"),sQuery(id+"F0.wireOp",EDGE,"E3"),sQuery(id+"F0.wireOp",EDGE,"E4.top"),sQuery(id+"F0.wireOp",EDGE,"E4.right"),sQuery(id+"F0.wireOp",EDGE,"E6"),sQuery(id+"F0.wireOp",EDGE,"E7.MirrorCS"),sQuery(id+"F0.wireOp",EDGE,"E8"),sQuery(id+"F0.wireOp",EDGE,"E9.MirrorCS"),sQuery(id+"F0.wireOp",EDGE,"E10"),subQ2,subQ1,subQ0,sQuery(id+"F0.wireOp",EDGE,"E13"),sQuery(id+"F0.wireOp",EDGE,"E14"),sQuery(id+"F0.wireOp",EDGE,"E15"),sQuery(id+"F0.wireOp",EDGE,"E16"),sQuery(id+"F0.wireOp",EDGE,"E17")])],"isStart":false})]});}
            var Q26;
            Q26=makeQuery(id+"F1.opExtrude","CAP_EDGE",EDGE,{"disambiguationData":[OSD([sQuery(id+"F0.wireOp",EDGE,"E12.top")])],"isStart":false});
            var Q27;
            {var subQ0=sQuery(id+"F0.wireOp",EDGE,"E13");var subQ1=sQuery(id+"F0.wireOp",EDGE,"E12.top");Q27=makeQuery(id+"F5.opFillet","BLEND_EDGE",EDGE,{"blendedFrom":[makeQuery(id+"F1.opExtrude","SWEPT_EDGE",EDGE,{"disambiguationData":[OSD([subQ1,subQ0])]}),makeQuery(id+"F1.opExtrude","CAP_FACE",FACE,{"disambiguationData":[OSD([sQuery(id+"F0.wireOp",EDGE,"E0.top"),sQuery(id+"F0.wireOp",EDGE,"E1.top"),sQuery(id+"F0.wireOp",EDGE,"E1.right"),sQuery(id+"F0.wireOp",EDGE,"E2"),sQuery(id+"F0.wireOp",EDGE,"E3"),sQuery(id+"F0.wireOp",EDGE,"E4.top"),sQuery(id+"F0.wireOp",EDGE,"E4.right"),sQuery(id+"F0.wireOp",EDGE,"E6"),sQuery(id+"F0.wireOp",EDGE,"E7.MirrorCS"),sQuery(id+"F0.wireOp",EDGE,"E8"),sQuery(id+"F0.wireOp",EDGE,"E9.MirrorCS"),sQuery(id+"F0.wireOp",EDGE,"E10"),sQuery(id+"F0.wireOp",EDGE,"E11.top"),subQ1,sQuery(id+"F0.wireOp",EDGE,"E12.right"),subQ0,sQuery(id+"F0.wireOp",EDGE,"E14"),sQuery(id+"F0.wireOp",EDGE,"E15"),sQuery(id+"F0.wireOp",EDGE,"E16"),sQuery(id+"F0.wireOp",EDGE,"E17")])],"isStart":false})],"blendedInto":[makeQuery(id+"F1.opExtrude","CAP_FACE",FACE,{"disambiguationData":[OSD([sQuery(id+"F0.wireOp",EDGE,"E0.top"),sQuery(id+"F0.wireOp",EDGE,"E1.top"),sQuery(id+"F0.wireOp",EDGE,"E1.right"),sQuery(id+"F0.wireOp",EDGE,"E2"),sQuery(id+"F0.wireOp",EDGE,"E3"),sQuery(id+"F0.wireOp",EDGE,"E4.top"),sQuery(id+"F0.wireOp",EDGE,"E4.right"),sQuery(id+"F0.wireOp",EDGE,"E6"),sQuery(id+"F0.wireOp",EDGE,"E7.MirrorCS"),sQuery(id+"F0.wireOp",EDGE,"E8"),sQuery(id+"F0.wireOp",EDGE,"E9.MirrorCS"),sQuery(id+"F0.wireOp",EDGE,"E10"),sQuery(id+"F0.wireOp",EDGE,"E11.top"),subQ1,sQuery(id+"F0.wireOp",EDGE,"E12.right"),subQ0,sQuery(id+"F0.wireOp",EDGE,"E14"),sQuery(id+"F0.wireOp",EDGE,"E15"),sQuery(id+"F0.wireOp",EDGE,"E16"),sQuery(id+"F0.wireOp",EDGE,"E17")])],"isStart":false})]});}
            var Q28;
            {var subQ0=sQuery(id+"F0.wireOp",EDGE,"E14");var subQ1=sQuery(id+"F0.wireOp",EDGE,"E13");Q28=makeQuery(id+"F6.opFillet","BLEND_EDGE",EDGE,{"blendedFrom":[makeQuery(id+"F1.opExtrude","SWEPT_EDGE",EDGE,{"disambiguationData":[OSD([subQ1,subQ0])]}),makeQuery(id+"F1.opExtrude","CAP_FACE",FACE,{"disambiguationData":[OSD([sQuery(id+"F0.wireOp",EDGE,"E0.top"),sQuery(id+"F0.wireOp",EDGE,"E1.top"),sQuery(id+"F0.wireOp",EDGE,"E1.right"),sQuery(id+"F0.wireOp",EDGE,"E2"),sQuery(id+"F0.wireOp",EDGE,"E3"),sQuery(id+"F0.wireOp",EDGE,"E4.top"),sQuery(id+"F0.wireOp",EDGE,"E4.right"),sQuery(id+"F0.wireOp",EDGE,"E6"),sQuery(id+"F0.wireOp",EDGE,"E7.MirrorCS"),sQuery(id+"F0.wireOp",EDGE,"E8"),sQuery(id+"F0.wireOp",EDGE,"E9.MirrorCS"),sQuery(id+"F0.wireOp",EDGE,"E10"),sQuery(id+"F0.wireOp",EDGE,"E11.top"),sQuery(id+"F0.wireOp",EDGE,"E12.top"),sQuery(id+"F0.wireOp",EDGE,"E12.right"),subQ1,subQ0,sQuery(id+"F0.wireOp",EDGE,"E15"),sQuery(id+"F0.wireOp",EDGE,"E16"),sQuery(id+"F0.wireOp",EDGE,"E17")])],"isStart":false})],"blendedInto":[makeQuery(id+"F1.opExtrude","CAP_FACE",FACE,{"disambiguationData":[OSD([sQuery(id+"F0.wireOp",EDGE,"E0.top"),sQuery(id+"F0.wireOp",EDGE,"E1.top"),sQuery(id+"F0.wireOp",EDGE,"E1.right"),sQuery(id+"F0.wireOp",EDGE,"E2"),sQuery(id+"F0.wireOp",EDGE,"E3"),sQuery(id+"F0.wireOp",EDGE,"E4.top"),sQuery(id+"F0.wireOp",EDGE,"E4.right"),sQuery(id+"F0.wireOp",EDGE,"E6"),sQuery(id+"F0.wireOp",EDGE,"E7.MirrorCS"),sQuery(id+"F0.wireOp",EDGE,"E8"),sQuery(id+"F0.wireOp",EDGE,"E9.MirrorCS"),sQuery(id+"F0.wireOp",EDGE,"E10"),sQuery(id+"F0.wireOp",EDGE,"E11.top"),sQuery(id+"F0.wireOp",EDGE,"E12.top"),sQuery(id+"F0.wireOp",EDGE,"E12.right"),subQ1,subQ0,sQuery(id+"F0.wireOp",EDGE,"E15"),sQuery(id+"F0.wireOp",EDGE,"E16"),sQuery(id+"F0.wireOp",EDGE,"E17")])],"isStart":false})]});}
            var Q29;
            Q29=makeQuery(id+"F1.opExtrude","CAP_EDGE",EDGE,{"disambiguationData":[OSD([sQuery(id+"F0.wireOp",EDGE,"E14")])],"isStart":false});
            fillet(context, id + "F20", {"entities" : qUnion([Q0, Q1, Q2, Q3, Q4, Q5, Q6, Q7, Q8, Q9, Q10, Q11, Q12, Q13, Q14, Q15, Q16, Q17, Q18, Q19, Q20, Q21, Q22, Q23, Q24, Q25, Q26, Q27, Q28, Q29]), "radius" : 0.5 * mm, "tangentPropagation" : true, "rho" : 0.5, "crossSection" : FilletCrossSection.CONIC, "allowEdgeOverflow" : false});
        }
    });
